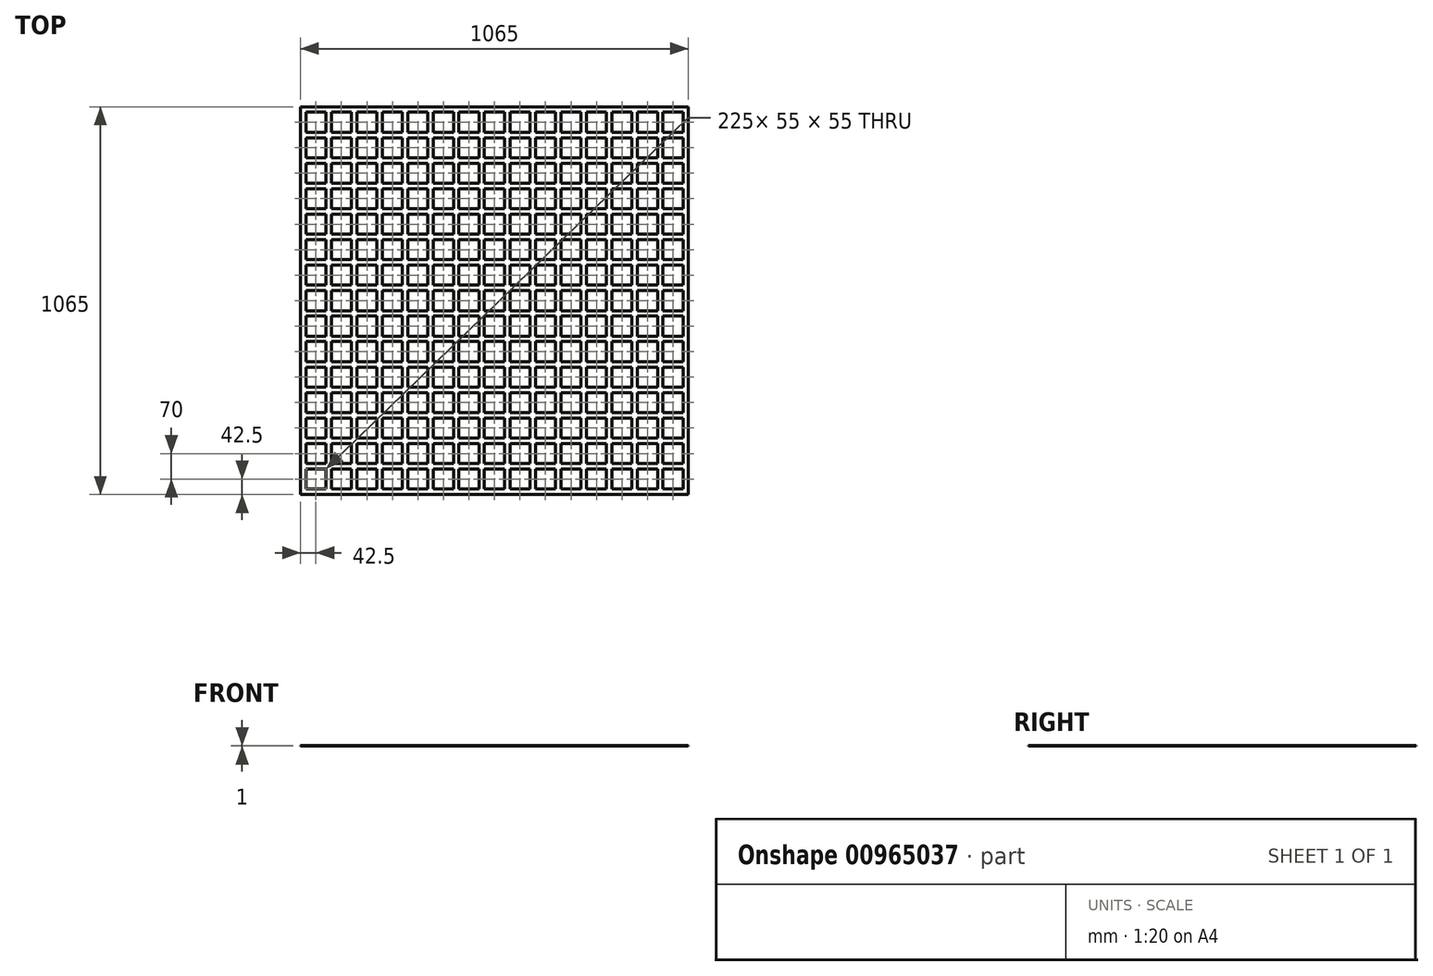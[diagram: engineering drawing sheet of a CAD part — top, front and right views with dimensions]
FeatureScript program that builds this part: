
annotation { "Feature Type Name" : "Feature", "Feature Type Description" : "" }
export const myFeature = defineFeature(function(context is Context, id is Id, definition is map)
    precondition{}
    {
        {
            var Q0;
            Q0=qCreatedBy(makeId("Top.planeOp"),FACE);
            var sketch = newSketch(context, id + "F0", { "sketchPlane" : qUnion([Q0])});
            skLineSegment(sketch, "E0.bottom", {"start": v(0, 0) * mm, "end": v(55, 0) * mm});
            skLineSegment(sketch, "E0.top", {"start": v(0, 55) * mm, "end": v(55, 55) * mm});
            skLineSegment(sketch, "E0.left", {"start": v(0, 0) * mm, "end": v(0, 55) * mm});
            skLineSegment(sketch, "E0.right", {"start": v(55, 0) * mm, "end": v(55, 55) * mm});
            skLineSegment(sketch, "E1.0.1.0", {"start": v(0, 70) * mm, "end": v(0, 125) * mm});
            skLineSegment(sketch, "E1.0.1.1", {"start": v(0, 125) * mm, "end": v(55, 125) * mm});
            skLineSegment(sketch, "E1.0.1.2", {"start": v(0, 70) * mm, "end": v(55, 70) * mm});
            skLineSegment(sketch, "E1.0.1.3", {"start": v(55, 70) * mm, "end": v(55, 125) * mm});
            skLineSegment(sketch, "E1.0.2.0", {"start": v(0, 140) * mm, "end": v(0, 195) * mm});
            skLineSegment(sketch, "E1.0.2.1", {"start": v(0, 195) * mm, "end": v(55, 195) * mm});
            skLineSegment(sketch, "E1.0.2.2", {"start": v(0, 140) * mm, "end": v(55, 140) * mm});
            skLineSegment(sketch, "E1.0.2.3", {"start": v(55, 140) * mm, "end": v(55, 195) * mm});
            skLineSegment(sketch, "E1.0.3.0", {"start": v(0, 210) * mm, "end": v(0, 265) * mm});
            skLineSegment(sketch, "E1.0.3.1", {"start": v(0, 265) * mm, "end": v(55, 265) * mm});
            skLineSegment(sketch, "E1.0.3.2", {"start": v(0, 210) * mm, "end": v(55, 210) * mm});
            skLineSegment(sketch, "E1.0.3.3", {"start": v(55, 210) * mm, "end": v(55, 265) * mm});
            skLineSegment(sketch, "E1.0.4.0", {"start": v(0, 280) * mm, "end": v(0, 335) * mm});
            skLineSegment(sketch, "E1.0.4.1", {"start": v(0, 335) * mm, "end": v(55, 335) * mm});
            skLineSegment(sketch, "E1.0.4.2", {"start": v(0, 280) * mm, "end": v(55, 280) * mm});
            skLineSegment(sketch, "E1.0.4.3", {"start": v(55, 280) * mm, "end": v(55, 335) * mm});
            skLineSegment(sketch, "E1.0.5.0", {"start": v(0, 350) * mm, "end": v(0, 405) * mm});
            skLineSegment(sketch, "E1.0.5.1", {"start": v(0, 405) * mm, "end": v(55, 405) * mm});
            skLineSegment(sketch, "E1.0.5.2", {"start": v(0, 350) * mm, "end": v(55, 350) * mm});
            skLineSegment(sketch, "E1.0.5.3", {"start": v(55, 350) * mm, "end": v(55, 405) * mm});
            skLineSegment(sketch, "E1.0.6.0", {"start": v(0, 420) * mm, "end": v(0, 475) * mm});
            skLineSegment(sketch, "E1.0.6.1", {"start": v(0, 475) * mm, "end": v(55, 475) * mm});
            skLineSegment(sketch, "E1.0.6.2", {"start": v(0, 420) * mm, "end": v(55, 420) * mm});
            skLineSegment(sketch, "E1.0.6.3", {"start": v(55, 420) * mm, "end": v(55, 475) * mm});
            skLineSegment(sketch, "E1.0.7.0", {"start": v(0, 490) * mm, "end": v(0, 545) * mm});
            skLineSegment(sketch, "E1.0.7.1", {"start": v(0, 545) * mm, "end": v(55, 545) * mm});
            skLineSegment(sketch, "E1.0.7.2", {"start": v(0, 490) * mm, "end": v(55, 490) * mm});
            skLineSegment(sketch, "E1.0.7.3", {"start": v(55, 490) * mm, "end": v(55, 545) * mm});
            skLineSegment(sketch, "E1.0.8.0", {"start": v(0, 560) * mm, "end": v(0, 615) * mm});
            skLineSegment(sketch, "E1.0.8.1", {"start": v(0, 615) * mm, "end": v(55, 615) * mm});
            skLineSegment(sketch, "E1.0.8.2", {"start": v(0, 560) * mm, "end": v(55, 560) * mm});
            skLineSegment(sketch, "E1.0.8.3", {"start": v(55, 560) * mm, "end": v(55, 615) * mm});
            skLineSegment(sketch, "E1.0.9.0", {"start": v(0, 630) * mm, "end": v(0, 685) * mm});
            skLineSegment(sketch, "E1.0.9.1", {"start": v(0, 685) * mm, "end": v(55, 685) * mm});
            skLineSegment(sketch, "E1.0.9.2", {"start": v(0, 630) * mm, "end": v(55, 630) * mm});
            skLineSegment(sketch, "E1.0.9.3", {"start": v(55, 630) * mm, "end": v(55, 685) * mm});
            skLineSegment(sketch, "E1.1.0.0", {"start": v(70, 0) * mm, "end": v(70, 55) * mm});
            skLineSegment(sketch, "E1.1.0.1", {"start": v(70, 55) * mm, "end": v(125, 55) * mm});
            skLineSegment(sketch, "E1.1.0.2", {"start": v(70, 0) * mm, "end": v(125, 0) * mm});
            skLineSegment(sketch, "E1.1.0.3", {"start": v(125, 0) * mm, "end": v(125, 55) * mm});
            skLineSegment(sketch, "E1.1.1.0", {"start": v(70, 70) * mm, "end": v(70, 125) * mm});
            skLineSegment(sketch, "E1.1.1.1", {"start": v(70, 125) * mm, "end": v(125, 125) * mm});
            skLineSegment(sketch, "E1.1.1.2", {"start": v(70, 70) * mm, "end": v(125, 70) * mm});
            skLineSegment(sketch, "E1.1.1.3", {"start": v(125, 70) * mm, "end": v(125, 125) * mm});
            skLineSegment(sketch, "E1.1.2.0", {"start": v(70, 140) * mm, "end": v(70, 195) * mm});
            skLineSegment(sketch, "E1.1.2.1", {"start": v(70, 195) * mm, "end": v(125, 195) * mm});
            skLineSegment(sketch, "E1.1.2.2", {"start": v(70, 140) * mm, "end": v(125, 140) * mm});
            skLineSegment(sketch, "E1.1.2.3", {"start": v(125, 140) * mm, "end": v(125, 195) * mm});
            skLineSegment(sketch, "E1.1.3.0", {"start": v(70, 210) * mm, "end": v(70, 265) * mm});
            skLineSegment(sketch, "E1.1.3.1", {"start": v(70, 265) * mm, "end": v(125, 265) * mm});
            skLineSegment(sketch, "E1.1.3.2", {"start": v(70, 210) * mm, "end": v(125, 210) * mm});
            skLineSegment(sketch, "E1.1.3.3", {"start": v(125, 210) * mm, "end": v(125, 265) * mm});
            skLineSegment(sketch, "E1.1.4.0", {"start": v(70, 280) * mm, "end": v(70, 335) * mm});
            skLineSegment(sketch, "E1.1.4.1", {"start": v(70, 335) * mm, "end": v(125, 335) * mm});
            skLineSegment(sketch, "E1.1.4.2", {"start": v(70, 280) * mm, "end": v(125, 280) * mm});
            skLineSegment(sketch, "E1.1.4.3", {"start": v(125, 280) * mm, "end": v(125, 335) * mm});
            skLineSegment(sketch, "E1.1.5.0", {"start": v(70, 350) * mm, "end": v(70, 405) * mm});
            skLineSegment(sketch, "E1.1.5.1", {"start": v(70, 405) * mm, "end": v(125, 405) * mm});
            skLineSegment(sketch, "E1.1.5.2", {"start": v(70, 350) * mm, "end": v(125, 350) * mm});
            skLineSegment(sketch, "E1.1.5.3", {"start": v(125, 350) * mm, "end": v(125, 405) * mm});
            skLineSegment(sketch, "E1.1.6.0", {"start": v(70, 420) * mm, "end": v(70, 475) * mm});
            skLineSegment(sketch, "E1.1.6.1", {"start": v(70, 475) * mm, "end": v(125, 475) * mm});
            skLineSegment(sketch, "E1.1.6.2", {"start": v(70, 420) * mm, "end": v(125, 420) * mm});
            skLineSegment(sketch, "E1.1.6.3", {"start": v(125, 420) * mm, "end": v(125, 475) * mm});
            skLineSegment(sketch, "E1.1.7.0", {"start": v(70, 490) * mm, "end": v(70, 545) * mm});
            skLineSegment(sketch, "E1.1.7.1", {"start": v(70, 545) * mm, "end": v(125, 545) * mm});
            skLineSegment(sketch, "E1.1.7.2", {"start": v(70, 490) * mm, "end": v(125, 490) * mm});
            skLineSegment(sketch, "E1.1.7.3", {"start": v(125, 490) * mm, "end": v(125, 545) * mm});
            skLineSegment(sketch, "E1.1.8.0", {"start": v(70, 560) * mm, "end": v(70, 615) * mm});
            skLineSegment(sketch, "E1.1.8.1", {"start": v(70, 615) * mm, "end": v(125, 615) * mm});
            skLineSegment(sketch, "E1.1.8.2", {"start": v(70, 560) * mm, "end": v(125, 560) * mm});
            skLineSegment(sketch, "E1.1.8.3", {"start": v(125, 560) * mm, "end": v(125, 615) * mm});
            skLineSegment(sketch, "E1.1.9.0", {"start": v(70, 630) * mm, "end": v(70, 685) * mm});
            skLineSegment(sketch, "E1.1.9.1", {"start": v(70, 685) * mm, "end": v(125, 685) * mm});
            skLineSegment(sketch, "E1.1.9.2", {"start": v(70, 630) * mm, "end": v(125, 630) * mm});
            skLineSegment(sketch, "E1.1.9.3", {"start": v(125, 630) * mm, "end": v(125, 685) * mm});
            skLineSegment(sketch, "E1.2.0.0", {"start": v(140, 0) * mm, "end": v(140, 55) * mm});
            skLineSegment(sketch, "E1.2.0.1", {"start": v(140, 55) * mm, "end": v(195, 55) * mm});
            skLineSegment(sketch, "E1.2.0.2", {"start": v(140, 0) * mm, "end": v(195, 0) * mm});
            skLineSegment(sketch, "E1.2.0.3", {"start": v(195, 0) * mm, "end": v(195, 55) * mm});
            skLineSegment(sketch, "E1.2.1.0", {"start": v(140, 70) * mm, "end": v(140, 125) * mm});
            skLineSegment(sketch, "E1.2.1.1", {"start": v(140, 125) * mm, "end": v(195, 125) * mm});
            skLineSegment(sketch, "E1.2.1.2", {"start": v(140, 70) * mm, "end": v(195, 70) * mm});
            skLineSegment(sketch, "E1.2.1.3", {"start": v(195, 70) * mm, "end": v(195, 125) * mm});
            skLineSegment(sketch, "E1.2.2.0", {"start": v(140, 140) * mm, "end": v(140, 195) * mm});
            skLineSegment(sketch, "E1.2.2.1", {"start": v(140, 195) * mm, "end": v(195, 195) * mm});
            skLineSegment(sketch, "E1.2.2.2", {"start": v(140, 140) * mm, "end": v(195, 140) * mm});
            skLineSegment(sketch, "E1.2.2.3", {"start": v(195, 140) * mm, "end": v(195, 195) * mm});
            skLineSegment(sketch, "E1.2.3.0", {"start": v(140, 210) * mm, "end": v(140, 265) * mm});
            skLineSegment(sketch, "E1.2.3.1", {"start": v(140, 265) * mm, "end": v(195, 265) * mm});
            skLineSegment(sketch, "E1.2.3.2", {"start": v(140, 210) * mm, "end": v(195, 210) * mm});
            skLineSegment(sketch, "E1.2.3.3", {"start": v(195, 210) * mm, "end": v(195, 265) * mm});
            skLineSegment(sketch, "E1.2.4.0", {"start": v(140, 280) * mm, "end": v(140, 335) * mm});
            skLineSegment(sketch, "E1.2.4.1", {"start": v(140, 335) * mm, "end": v(195, 335) * mm});
            skLineSegment(sketch, "E1.2.4.2", {"start": v(140, 280) * mm, "end": v(195, 280) * mm});
            skLineSegment(sketch, "E1.2.4.3", {"start": v(195, 280) * mm, "end": v(195, 335) * mm});
            skLineSegment(sketch, "E1.2.5.0", {"start": v(140, 350) * mm, "end": v(140, 405) * mm});
            skLineSegment(sketch, "E1.2.5.1", {"start": v(140, 405) * mm, "end": v(195, 405) * mm});
            skLineSegment(sketch, "E1.2.5.2", {"start": v(140, 350) * mm, "end": v(195, 350) * mm});
            skLineSegment(sketch, "E1.2.5.3", {"start": v(195, 350) * mm, "end": v(195, 405) * mm});
            skLineSegment(sketch, "E1.2.6.0", {"start": v(140, 420) * mm, "end": v(140, 475) * mm});
            skLineSegment(sketch, "E1.2.6.1", {"start": v(140, 475) * mm, "end": v(195, 475) * mm});
            skLineSegment(sketch, "E1.2.6.2", {"start": v(140, 420) * mm, "end": v(195, 420) * mm});
            skLineSegment(sketch, "E1.2.6.3", {"start": v(195, 420) * mm, "end": v(195, 475) * mm});
            skLineSegment(sketch, "E1.2.7.0", {"start": v(140, 490) * mm, "end": v(140, 545) * mm});
            skLineSegment(sketch, "E1.2.7.1", {"start": v(140, 545) * mm, "end": v(195, 545) * mm});
            skLineSegment(sketch, "E1.2.7.2", {"start": v(140, 490) * mm, "end": v(195, 490) * mm});
            skLineSegment(sketch, "E1.2.7.3", {"start": v(195, 490) * mm, "end": v(195, 545) * mm});
            skLineSegment(sketch, "E1.2.8.0", {"start": v(140, 560) * mm, "end": v(140, 615) * mm});
            skLineSegment(sketch, "E1.2.8.1", {"start": v(140, 615) * mm, "end": v(195, 615) * mm});
            skLineSegment(sketch, "E1.2.8.2", {"start": v(140, 560) * mm, "end": v(195, 560) * mm});
            skLineSegment(sketch, "E1.2.8.3", {"start": v(195, 560) * mm, "end": v(195, 615) * mm});
            skLineSegment(sketch, "E1.2.9.0", {"start": v(140, 630) * mm, "end": v(140, 685) * mm});
            skLineSegment(sketch, "E1.2.9.1", {"start": v(140, 685) * mm, "end": v(195, 685) * mm});
            skLineSegment(sketch, "E1.2.9.2", {"start": v(140, 630) * mm, "end": v(195, 630) * mm});
            skLineSegment(sketch, "E1.2.9.3", {"start": v(195, 630) * mm, "end": v(195, 685) * mm});
            skLineSegment(sketch, "E1.3.0.0", {"start": v(210, 0) * mm, "end": v(210, 55) * mm});
            skLineSegment(sketch, "E1.3.0.1", {"start": v(210, 55) * mm, "end": v(265, 55) * mm});
            skLineSegment(sketch, "E1.3.0.2", {"start": v(210, 0) * mm, "end": v(265, 0) * mm});
            skLineSegment(sketch, "E1.3.0.3", {"start": v(265, 0) * mm, "end": v(265, 55) * mm});
            skLineSegment(sketch, "E1.3.1.0", {"start": v(210, 70) * mm, "end": v(210, 125) * mm});
            skLineSegment(sketch, "E1.3.1.1", {"start": v(210, 125) * mm, "end": v(265, 125) * mm});
            skLineSegment(sketch, "E1.3.1.2", {"start": v(210, 70) * mm, "end": v(265, 70) * mm});
            skLineSegment(sketch, "E1.3.1.3", {"start": v(265, 70) * mm, "end": v(265, 125) * mm});
            skLineSegment(sketch, "E1.3.2.0", {"start": v(210, 140) * mm, "end": v(210, 195) * mm});
            skLineSegment(sketch, "E1.3.2.1", {"start": v(210, 195) * mm, "end": v(265, 195) * mm});
            skLineSegment(sketch, "E1.3.2.2", {"start": v(210, 140) * mm, "end": v(265, 140) * mm});
            skLineSegment(sketch, "E1.3.2.3", {"start": v(265, 140) * mm, "end": v(265, 195) * mm});
            skLineSegment(sketch, "E1.3.3.0", {"start": v(210, 210) * mm, "end": v(210, 265) * mm});
            skLineSegment(sketch, "E1.3.3.1", {"start": v(210, 265) * mm, "end": v(265, 265) * mm});
            skLineSegment(sketch, "E1.3.3.2", {"start": v(210, 210) * mm, "end": v(265, 210) * mm});
            skLineSegment(sketch, "E1.3.3.3", {"start": v(265, 210) * mm, "end": v(265, 265) * mm});
            skLineSegment(sketch, "E1.3.4.0", {"start": v(210, 280) * mm, "end": v(210, 335) * mm});
            skLineSegment(sketch, "E1.3.4.1", {"start": v(210, 335) * mm, "end": v(265, 335) * mm});
            skLineSegment(sketch, "E1.3.4.2", {"start": v(210, 280) * mm, "end": v(265, 280) * mm});
            skLineSegment(sketch, "E1.3.4.3", {"start": v(265, 280) * mm, "end": v(265, 335) * mm});
            skLineSegment(sketch, "E1.3.5.0", {"start": v(210, 350) * mm, "end": v(210, 405) * mm});
            skLineSegment(sketch, "E1.3.5.1", {"start": v(210, 405) * mm, "end": v(265, 405) * mm});
            skLineSegment(sketch, "E1.3.5.2", {"start": v(210, 350) * mm, "end": v(265, 350) * mm});
            skLineSegment(sketch, "E1.3.5.3", {"start": v(265, 350) * mm, "end": v(265, 405) * mm});
            skLineSegment(sketch, "E1.3.6.0", {"start": v(210, 420) * mm, "end": v(210, 475) * mm});
            skLineSegment(sketch, "E1.3.6.1", {"start": v(210, 475) * mm, "end": v(265, 475) * mm});
            skLineSegment(sketch, "E1.3.6.2", {"start": v(210, 420) * mm, "end": v(265, 420) * mm});
            skLineSegment(sketch, "E1.3.6.3", {"start": v(265, 420) * mm, "end": v(265, 475) * mm});
            skLineSegment(sketch, "E1.3.7.0", {"start": v(210, 490) * mm, "end": v(210, 545) * mm});
            skLineSegment(sketch, "E1.3.7.1", {"start": v(210, 545) * mm, "end": v(265, 545) * mm});
            skLineSegment(sketch, "E1.3.7.2", {"start": v(210, 490) * mm, "end": v(265, 490) * mm});
            skLineSegment(sketch, "E1.3.7.3", {"start": v(265, 490) * mm, "end": v(265, 545) * mm});
            skLineSegment(sketch, "E1.3.8.0", {"start": v(210, 560) * mm, "end": v(210, 615) * mm});
            skLineSegment(sketch, "E1.3.8.1", {"start": v(210, 615) * mm, "end": v(265, 615) * mm});
            skLineSegment(sketch, "E1.3.8.2", {"start": v(210, 560) * mm, "end": v(265, 560) * mm});
            skLineSegment(sketch, "E1.3.8.3", {"start": v(265, 560) * mm, "end": v(265, 615) * mm});
            skLineSegment(sketch, "E1.3.9.0", {"start": v(210, 630) * mm, "end": v(210, 685) * mm});
            skLineSegment(sketch, "E1.3.9.1", {"start": v(210, 685) * mm, "end": v(265, 685) * mm});
            skLineSegment(sketch, "E1.3.9.2", {"start": v(210, 630) * mm, "end": v(265, 630) * mm});
            skLineSegment(sketch, "E1.3.9.3", {"start": v(265, 630) * mm, "end": v(265, 685) * mm});
            skLineSegment(sketch, "E1.4.0.0", {"start": v(280, 0) * mm, "end": v(280, 55) * mm});
            skLineSegment(sketch, "E1.4.0.1", {"start": v(280, 55) * mm, "end": v(335, 55) * mm});
            skLineSegment(sketch, "E1.4.0.2", {"start": v(280, 0) * mm, "end": v(335, 0) * mm});
            skLineSegment(sketch, "E1.4.0.3", {"start": v(335, 0) * mm, "end": v(335, 55) * mm});
            skLineSegment(sketch, "E1.4.1.0", {"start": v(280, 70) * mm, "end": v(280, 125) * mm});
            skLineSegment(sketch, "E1.4.1.1", {"start": v(280, 125) * mm, "end": v(335, 125) * mm});
            skLineSegment(sketch, "E1.4.1.2", {"start": v(280, 70) * mm, "end": v(335, 70) * mm});
            skLineSegment(sketch, "E1.4.1.3", {"start": v(335, 70) * mm, "end": v(335, 125) * mm});
            skLineSegment(sketch, "E1.4.2.0", {"start": v(280, 140) * mm, "end": v(280, 195) * mm});
            skLineSegment(sketch, "E1.4.2.1", {"start": v(280, 195) * mm, "end": v(335, 195) * mm});
            skLineSegment(sketch, "E1.4.2.2", {"start": v(280, 140) * mm, "end": v(335, 140) * mm});
            skLineSegment(sketch, "E1.4.2.3", {"start": v(335, 140) * mm, "end": v(335, 195) * mm});
            skLineSegment(sketch, "E1.4.3.0", {"start": v(280, 210) * mm, "end": v(280, 265) * mm});
            skLineSegment(sketch, "E1.4.3.1", {"start": v(280, 265) * mm, "end": v(335, 265) * mm});
            skLineSegment(sketch, "E1.4.3.2", {"start": v(280, 210) * mm, "end": v(335, 210) * mm});
            skLineSegment(sketch, "E1.4.3.3", {"start": v(335, 210) * mm, "end": v(335, 265) * mm});
            skLineSegment(sketch, "E1.4.4.0", {"start": v(280, 280) * mm, "end": v(280, 335) * mm});
            skLineSegment(sketch, "E1.4.4.1", {"start": v(280, 335) * mm, "end": v(335, 335) * mm});
            skLineSegment(sketch, "E1.4.4.2", {"start": v(280, 280) * mm, "end": v(335, 280) * mm});
            skLineSegment(sketch, "E1.4.4.3", {"start": v(335, 280) * mm, "end": v(335, 335) * mm});
            skLineSegment(sketch, "E1.4.5.0", {"start": v(280, 350) * mm, "end": v(280, 405) * mm});
            skLineSegment(sketch, "E1.4.5.1", {"start": v(280, 405) * mm, "end": v(335, 405) * mm});
            skLineSegment(sketch, "E1.4.5.2", {"start": v(280, 350) * mm, "end": v(335, 350) * mm});
            skLineSegment(sketch, "E1.4.5.3", {"start": v(335, 350) * mm, "end": v(335, 405) * mm});
            skLineSegment(sketch, "E1.4.6.0", {"start": v(280, 420) * mm, "end": v(280, 475) * mm});
            skLineSegment(sketch, "E1.4.6.1", {"start": v(280, 475) * mm, "end": v(335, 475) * mm});
            skLineSegment(sketch, "E1.4.6.2", {"start": v(280, 420) * mm, "end": v(335, 420) * mm});
            skLineSegment(sketch, "E1.4.6.3", {"start": v(335, 420) * mm, "end": v(335, 475) * mm});
            skLineSegment(sketch, "E1.4.7.0", {"start": v(280, 490) * mm, "end": v(280, 545) * mm});
            skLineSegment(sketch, "E1.4.7.1", {"start": v(280, 545) * mm, "end": v(335, 545) * mm});
            skLineSegment(sketch, "E1.4.7.2", {"start": v(280, 490) * mm, "end": v(335, 490) * mm});
            skLineSegment(sketch, "E1.4.7.3", {"start": v(335, 490) * mm, "end": v(335, 545) * mm});
            skLineSegment(sketch, "E1.4.8.0", {"start": v(280, 560) * mm, "end": v(280, 615) * mm});
            skLineSegment(sketch, "E1.4.8.1", {"start": v(280, 615) * mm, "end": v(335, 615) * mm});
            skLineSegment(sketch, "E1.4.8.2", {"start": v(280, 560) * mm, "end": v(335, 560) * mm});
            skLineSegment(sketch, "E1.4.8.3", {"start": v(335, 560) * mm, "end": v(335, 615) * mm});
            skLineSegment(sketch, "E1.4.9.0", {"start": v(280, 630) * mm, "end": v(280, 685) * mm});
            skLineSegment(sketch, "E1.4.9.1", {"start": v(280, 685) * mm, "end": v(335, 685) * mm});
            skLineSegment(sketch, "E1.4.9.2", {"start": v(280, 630) * mm, "end": v(335, 630) * mm});
            skLineSegment(sketch, "E1.4.9.3", {"start": v(335, 630) * mm, "end": v(335, 685) * mm});
            skLineSegment(sketch, "E1.5.0.0", {"start": v(350, 0) * mm, "end": v(350, 55) * mm});
            skLineSegment(sketch, "E1.5.0.1", {"start": v(350, 55) * mm, "end": v(405, 55) * mm});
            skLineSegment(sketch, "E1.5.0.2", {"start": v(350, 0) * mm, "end": v(405, 0) * mm});
            skLineSegment(sketch, "E1.5.0.3", {"start": v(405, 0) * mm, "end": v(405, 55) * mm});
            skLineSegment(sketch, "E1.5.1.0", {"start": v(350, 70) * mm, "end": v(350, 125) * mm});
            skLineSegment(sketch, "E1.5.1.1", {"start": v(350, 125) * mm, "end": v(405, 125) * mm});
            skLineSegment(sketch, "E1.5.1.2", {"start": v(350, 70) * mm, "end": v(405, 70) * mm});
            skLineSegment(sketch, "E1.5.1.3", {"start": v(405, 70) * mm, "end": v(405, 125) * mm});
            skLineSegment(sketch, "E1.5.2.0", {"start": v(350, 140) * mm, "end": v(350, 195) * mm});
            skLineSegment(sketch, "E1.5.2.1", {"start": v(350, 195) * mm, "end": v(405, 195) * mm});
            skLineSegment(sketch, "E1.5.2.2", {"start": v(350, 140) * mm, "end": v(405, 140) * mm});
            skLineSegment(sketch, "E1.5.2.3", {"start": v(405, 140) * mm, "end": v(405, 195) * mm});
            skLineSegment(sketch, "E1.5.3.0", {"start": v(350, 210) * mm, "end": v(350, 265) * mm});
            skLineSegment(sketch, "E1.5.3.1", {"start": v(350, 265) * mm, "end": v(405, 265) * mm});
            skLineSegment(sketch, "E1.5.3.2", {"start": v(350, 210) * mm, "end": v(405, 210) * mm});
            skLineSegment(sketch, "E1.5.3.3", {"start": v(405, 210) * mm, "end": v(405, 265) * mm});
            skLineSegment(sketch, "E1.5.4.0", {"start": v(350, 280) * mm, "end": v(350, 335) * mm});
            skLineSegment(sketch, "E1.5.4.1", {"start": v(350, 335) * mm, "end": v(405, 335) * mm});
            skLineSegment(sketch, "E1.5.4.2", {"start": v(350, 280) * mm, "end": v(405, 280) * mm});
            skLineSegment(sketch, "E1.5.4.3", {"start": v(405, 280) * mm, "end": v(405, 335) * mm});
            skLineSegment(sketch, "E1.5.5.0", {"start": v(350, 350) * mm, "end": v(350, 405) * mm});
            skLineSegment(sketch, "E1.5.5.1", {"start": v(350, 405) * mm, "end": v(405, 405) * mm});
            skLineSegment(sketch, "E1.5.5.2", {"start": v(350, 350) * mm, "end": v(405, 350) * mm});
            skLineSegment(sketch, "E1.5.5.3", {"start": v(405, 350) * mm, "end": v(405, 405) * mm});
            skLineSegment(sketch, "E1.5.6.0", {"start": v(350, 420) * mm, "end": v(350, 475) * mm});
            skLineSegment(sketch, "E1.5.6.1", {"start": v(350, 475) * mm, "end": v(405, 475) * mm});
            skLineSegment(sketch, "E1.5.6.2", {"start": v(350, 420) * mm, "end": v(405, 420) * mm});
            skLineSegment(sketch, "E1.5.6.3", {"start": v(405, 420) * mm, "end": v(405, 475) * mm});
            skLineSegment(sketch, "E1.5.7.0", {"start": v(350, 490) * mm, "end": v(350, 545) * mm});
            skLineSegment(sketch, "E1.5.7.1", {"start": v(350, 545) * mm, "end": v(405, 545) * mm});
            skLineSegment(sketch, "E1.5.7.2", {"start": v(350, 490) * mm, "end": v(405, 490) * mm});
            skLineSegment(sketch, "E1.5.7.3", {"start": v(405, 490) * mm, "end": v(405, 545) * mm});
            skLineSegment(sketch, "E1.5.8.0", {"start": v(350, 560) * mm, "end": v(350, 615) * mm});
            skLineSegment(sketch, "E1.5.8.1", {"start": v(350, 615) * mm, "end": v(405, 615) * mm});
            skLineSegment(sketch, "E1.5.8.2", {"start": v(350, 560) * mm, "end": v(405, 560) * mm});
            skLineSegment(sketch, "E1.5.8.3", {"start": v(405, 560) * mm, "end": v(405, 615) * mm});
            skLineSegment(sketch, "E1.5.9.0", {"start": v(350, 630) * mm, "end": v(350, 685) * mm});
            skLineSegment(sketch, "E1.5.9.1", {"start": v(350, 685) * mm, "end": v(405, 685) * mm});
            skLineSegment(sketch, "E1.5.9.2", {"start": v(350, 630) * mm, "end": v(405, 630) * mm});
            skLineSegment(sketch, "E1.5.9.3", {"start": v(405, 630) * mm, "end": v(405, 685) * mm});
            skLineSegment(sketch, "E1.6.0.0", {"start": v(420, 0) * mm, "end": v(420, 55) * mm});
            skLineSegment(sketch, "E1.6.0.1", {"start": v(420, 55) * mm, "end": v(475, 55) * mm});
            skLineSegment(sketch, "E1.6.0.2", {"start": v(420, 0) * mm, "end": v(475, 0) * mm});
            skLineSegment(sketch, "E1.6.0.3", {"start": v(475, 0) * mm, "end": v(475, 55) * mm});
            skLineSegment(sketch, "E1.6.1.0", {"start": v(420, 70) * mm, "end": v(420, 125) * mm});
            skLineSegment(sketch, "E1.6.1.1", {"start": v(420, 125) * mm, "end": v(475, 125) * mm});
            skLineSegment(sketch, "E1.6.1.2", {"start": v(420, 70) * mm, "end": v(475, 70) * mm});
            skLineSegment(sketch, "E1.6.1.3", {"start": v(475, 70) * mm, "end": v(475, 125) * mm});
            skLineSegment(sketch, "E1.6.2.0", {"start": v(420, 140) * mm, "end": v(420, 195) * mm});
            skLineSegment(sketch, "E1.6.2.1", {"start": v(420, 195) * mm, "end": v(475, 195) * mm});
            skLineSegment(sketch, "E1.6.2.2", {"start": v(420, 140) * mm, "end": v(475, 140) * mm});
            skLineSegment(sketch, "E1.6.2.3", {"start": v(475, 140) * mm, "end": v(475, 195) * mm});
            skLineSegment(sketch, "E1.6.3.0", {"start": v(420, 210) * mm, "end": v(420, 265) * mm});
            skLineSegment(sketch, "E1.6.3.1", {"start": v(420, 265) * mm, "end": v(475, 265) * mm});
            skLineSegment(sketch, "E1.6.3.2", {"start": v(420, 210) * mm, "end": v(475, 210) * mm});
            skLineSegment(sketch, "E1.6.3.3", {"start": v(475, 210) * mm, "end": v(475, 265) * mm});
            skLineSegment(sketch, "E1.6.4.0", {"start": v(420, 280) * mm, "end": v(420, 335) * mm});
            skLineSegment(sketch, "E1.6.4.1", {"start": v(420, 335) * mm, "end": v(475, 335) * mm});
            skLineSegment(sketch, "E1.6.4.2", {"start": v(420, 280) * mm, "end": v(475, 280) * mm});
            skLineSegment(sketch, "E1.6.4.3", {"start": v(475, 280) * mm, "end": v(475, 335) * mm});
            skLineSegment(sketch, "E1.6.5.0", {"start": v(420, 350) * mm, "end": v(420, 405) * mm});
            skLineSegment(sketch, "E1.6.5.1", {"start": v(420, 405) * mm, "end": v(475, 405) * mm});
            skLineSegment(sketch, "E1.6.5.2", {"start": v(420, 350) * mm, "end": v(475, 350) * mm});
            skLineSegment(sketch, "E1.6.5.3", {"start": v(475, 350) * mm, "end": v(475, 405) * mm});
            skLineSegment(sketch, "E1.6.6.0", {"start": v(420, 420) * mm, "end": v(420, 475) * mm});
            skLineSegment(sketch, "E1.6.6.1", {"start": v(420, 475) * mm, "end": v(475, 475) * mm});
            skLineSegment(sketch, "E1.6.6.2", {"start": v(420, 420) * mm, "end": v(475, 420) * mm});
            skLineSegment(sketch, "E1.6.6.3", {"start": v(475, 420) * mm, "end": v(475, 475) * mm});
            skLineSegment(sketch, "E1.6.7.0", {"start": v(420, 490) * mm, "end": v(420, 545) * mm});
            skLineSegment(sketch, "E1.6.7.1", {"start": v(420, 545) * mm, "end": v(475, 545) * mm});
            skLineSegment(sketch, "E1.6.7.2", {"start": v(420, 490) * mm, "end": v(475, 490) * mm});
            skLineSegment(sketch, "E1.6.7.3", {"start": v(475, 490) * mm, "end": v(475, 545) * mm});
            skLineSegment(sketch, "E1.6.8.0", {"start": v(420, 560) * mm, "end": v(420, 615) * mm});
            skLineSegment(sketch, "E1.6.8.1", {"start": v(420, 615) * mm, "end": v(475, 615) * mm});
            skLineSegment(sketch, "E1.6.8.2", {"start": v(420, 560) * mm, "end": v(475, 560) * mm});
            skLineSegment(sketch, "E1.6.8.3", {"start": v(475, 560) * mm, "end": v(475, 615) * mm});
            skLineSegment(sketch, "E1.6.9.0", {"start": v(420, 630) * mm, "end": v(420, 685) * mm});
            skLineSegment(sketch, "E1.6.9.1", {"start": v(420, 685) * mm, "end": v(475, 685) * mm});
            skLineSegment(sketch, "E1.6.9.2", {"start": v(420, 630) * mm, "end": v(475, 630) * mm});
            skLineSegment(sketch, "E1.6.9.3", {"start": v(475, 630) * mm, "end": v(475, 685) * mm});
            skLineSegment(sketch, "E1.7.0.0", {"start": v(490, 0) * mm, "end": v(490, 55) * mm});
            skLineSegment(sketch, "E1.7.0.1", {"start": v(490, 55) * mm, "end": v(545, 55) * mm});
            skLineSegment(sketch, "E1.7.0.2", {"start": v(490, 0) * mm, "end": v(545, 0) * mm});
            skLineSegment(sketch, "E1.7.0.3", {"start": v(545, 0) * mm, "end": v(545, 55) * mm});
            skLineSegment(sketch, "E1.7.1.0", {"start": v(490, 70) * mm, "end": v(490, 125) * mm});
            skLineSegment(sketch, "E1.7.1.1", {"start": v(490, 125) * mm, "end": v(545, 125) * mm});
            skLineSegment(sketch, "E1.7.1.2", {"start": v(490, 70) * mm, "end": v(545, 70) * mm});
            skLineSegment(sketch, "E1.7.1.3", {"start": v(545, 70) * mm, "end": v(545, 125) * mm});
            skLineSegment(sketch, "E1.7.2.0", {"start": v(490, 140) * mm, "end": v(490, 195) * mm});
            skLineSegment(sketch, "E1.7.2.1", {"start": v(490, 195) * mm, "end": v(545, 195) * mm});
            skLineSegment(sketch, "E1.7.2.2", {"start": v(490, 140) * mm, "end": v(545, 140) * mm});
            skLineSegment(sketch, "E1.7.2.3", {"start": v(545, 140) * mm, "end": v(545, 195) * mm});
            skLineSegment(sketch, "E1.7.3.0", {"start": v(490, 210) * mm, "end": v(490, 265) * mm});
            skLineSegment(sketch, "E1.7.3.1", {"start": v(490, 265) * mm, "end": v(545, 265) * mm});
            skLineSegment(sketch, "E1.7.3.2", {"start": v(490, 210) * mm, "end": v(545, 210) * mm});
            skLineSegment(sketch, "E1.7.3.3", {"start": v(545, 210) * mm, "end": v(545, 265) * mm});
            skLineSegment(sketch, "E1.7.4.0", {"start": v(490, 280) * mm, "end": v(490, 335) * mm});
            skLineSegment(sketch, "E1.7.4.1", {"start": v(490, 335) * mm, "end": v(545, 335) * mm});
            skLineSegment(sketch, "E1.7.4.2", {"start": v(490, 280) * mm, "end": v(545, 280) * mm});
            skLineSegment(sketch, "E1.7.4.3", {"start": v(545, 280) * mm, "end": v(545, 335) * mm});
            skLineSegment(sketch, "E1.7.5.0", {"start": v(490, 350) * mm, "end": v(490, 405) * mm});
            skLineSegment(sketch, "E1.7.5.1", {"start": v(490, 405) * mm, "end": v(545, 405) * mm});
            skLineSegment(sketch, "E1.7.5.2", {"start": v(490, 350) * mm, "end": v(545, 350) * mm});
            skLineSegment(sketch, "E1.7.5.3", {"start": v(545, 350) * mm, "end": v(545, 405) * mm});
            skLineSegment(sketch, "E1.7.6.0", {"start": v(490, 420) * mm, "end": v(490, 475) * mm});
            skLineSegment(sketch, "E1.7.6.1", {"start": v(490, 475) * mm, "end": v(545, 475) * mm});
            skLineSegment(sketch, "E1.7.6.2", {"start": v(490, 420) * mm, "end": v(545, 420) * mm});
            skLineSegment(sketch, "E1.7.6.3", {"start": v(545, 420) * mm, "end": v(545, 475) * mm});
            skLineSegment(sketch, "E1.7.7.0", {"start": v(490, 490) * mm, "end": v(490, 545) * mm});
            skLineSegment(sketch, "E1.7.7.1", {"start": v(490, 545) * mm, "end": v(545, 545) * mm});
            skLineSegment(sketch, "E1.7.7.2", {"start": v(490, 490) * mm, "end": v(545, 490) * mm});
            skLineSegment(sketch, "E1.7.7.3", {"start": v(545, 490) * mm, "end": v(545, 545) * mm});
            skLineSegment(sketch, "E1.7.8.0", {"start": v(490, 560) * mm, "end": v(490, 615) * mm});
            skLineSegment(sketch, "E1.7.8.1", {"start": v(490, 615) * mm, "end": v(545, 615) * mm});
            skLineSegment(sketch, "E1.7.8.2", {"start": v(490, 560) * mm, "end": v(545, 560) * mm});
            skLineSegment(sketch, "E1.7.8.3", {"start": v(545, 560) * mm, "end": v(545, 615) * mm});
            skLineSegment(sketch, "E1.7.9.0", {"start": v(490, 630) * mm, "end": v(490, 685) * mm});
            skLineSegment(sketch, "E1.7.9.1", {"start": v(490, 685) * mm, "end": v(545, 685) * mm});
            skLineSegment(sketch, "E1.7.9.2", {"start": v(490, 630) * mm, "end": v(545, 630) * mm});
            skLineSegment(sketch, "E1.7.9.3", {"start": v(545, 630) * mm, "end": v(545, 685) * mm});
            skLineSegment(sketch, "E1.8.0.0", {"start": v(560, 0) * mm, "end": v(560, 55) * mm});
            skLineSegment(sketch, "E1.8.0.1", {"start": v(560, 55) * mm, "end": v(615, 55) * mm});
            skLineSegment(sketch, "E1.8.0.2", {"start": v(560, 0) * mm, "end": v(615, 0) * mm});
            skLineSegment(sketch, "E1.8.0.3", {"start": v(615, 0) * mm, "end": v(615, 55) * mm});
            skLineSegment(sketch, "E1.8.1.0", {"start": v(560, 70) * mm, "end": v(560, 125) * mm});
            skLineSegment(sketch, "E1.8.1.1", {"start": v(560, 125) * mm, "end": v(615, 125) * mm});
            skLineSegment(sketch, "E1.8.1.2", {"start": v(560, 70) * mm, "end": v(615, 70) * mm});
            skLineSegment(sketch, "E1.8.1.3", {"start": v(615, 70) * mm, "end": v(615, 125) * mm});
            skLineSegment(sketch, "E1.8.2.0", {"start": v(560, 140) * mm, "end": v(560, 195) * mm});
            skLineSegment(sketch, "E1.8.2.1", {"start": v(560, 195) * mm, "end": v(615, 195) * mm});
            skLineSegment(sketch, "E1.8.2.2", {"start": v(560, 140) * mm, "end": v(615, 140) * mm});
            skLineSegment(sketch, "E1.8.2.3", {"start": v(615, 140) * mm, "end": v(615, 195) * mm});
            skLineSegment(sketch, "E1.8.3.0", {"start": v(560, 210) * mm, "end": v(560, 265) * mm});
            skLineSegment(sketch, "E1.8.3.1", {"start": v(560, 265) * mm, "end": v(615, 265) * mm});
            skLineSegment(sketch, "E1.8.3.2", {"start": v(560, 210) * mm, "end": v(615, 210) * mm});
            skLineSegment(sketch, "E1.8.3.3", {"start": v(615, 210) * mm, "end": v(615, 265) * mm});
            skLineSegment(sketch, "E1.8.4.0", {"start": v(560, 280) * mm, "end": v(560, 335) * mm});
            skLineSegment(sketch, "E1.8.4.1", {"start": v(560, 335) * mm, "end": v(615, 335) * mm});
            skLineSegment(sketch, "E1.8.4.2", {"start": v(560, 280) * mm, "end": v(615, 280) * mm});
            skLineSegment(sketch, "E1.8.4.3", {"start": v(615, 280) * mm, "end": v(615, 335) * mm});
            skLineSegment(sketch, "E1.8.5.0", {"start": v(560, 350) * mm, "end": v(560, 405) * mm});
            skLineSegment(sketch, "E1.8.5.1", {"start": v(560, 405) * mm, "end": v(615, 405) * mm});
            skLineSegment(sketch, "E1.8.5.2", {"start": v(560, 350) * mm, "end": v(615, 350) * mm});
            skLineSegment(sketch, "E1.8.5.3", {"start": v(615, 350) * mm, "end": v(615, 405) * mm});
            skLineSegment(sketch, "E1.8.6.0", {"start": v(560, 420) * mm, "end": v(560, 475) * mm});
            skLineSegment(sketch, "E1.8.6.1", {"start": v(560, 475) * mm, "end": v(615, 475) * mm});
            skLineSegment(sketch, "E1.8.6.2", {"start": v(560, 420) * mm, "end": v(615, 420) * mm});
            skLineSegment(sketch, "E1.8.6.3", {"start": v(615, 420) * mm, "end": v(615, 475) * mm});
            skLineSegment(sketch, "E1.8.7.0", {"start": v(560, 490) * mm, "end": v(560, 545) * mm});
            skLineSegment(sketch, "E1.8.7.1", {"start": v(560, 545) * mm, "end": v(615, 545) * mm});
            skLineSegment(sketch, "E1.8.7.2", {"start": v(560, 490) * mm, "end": v(615, 490) * mm});
            skLineSegment(sketch, "E1.8.7.3", {"start": v(615, 490) * mm, "end": v(615, 545) * mm});
            skLineSegment(sketch, "E1.8.8.0", {"start": v(560, 560) * mm, "end": v(560, 615) * mm});
            skLineSegment(sketch, "E1.8.8.1", {"start": v(560, 615) * mm, "end": v(615, 615) * mm});
            skLineSegment(sketch, "E1.8.8.2", {"start": v(560, 560) * mm, "end": v(615, 560) * mm});
            skLineSegment(sketch, "E1.8.8.3", {"start": v(615, 560) * mm, "end": v(615, 615) * mm});
            skLineSegment(sketch, "E1.8.9.0", {"start": v(560, 630) * mm, "end": v(560, 685) * mm});
            skLineSegment(sketch, "E1.8.9.1", {"start": v(560, 685) * mm, "end": v(615, 685) * mm});
            skLineSegment(sketch, "E1.8.9.2", {"start": v(560, 630) * mm, "end": v(615, 630) * mm});
            skLineSegment(sketch, "E1.8.9.3", {"start": v(615, 630) * mm, "end": v(615, 685) * mm});
            skLineSegment(sketch, "E1.9.0.0", {"start": v(630, 0) * mm, "end": v(630, 55) * mm});
            skLineSegment(sketch, "E1.9.0.1", {"start": v(630, 55) * mm, "end": v(685, 55) * mm});
            skLineSegment(sketch, "E1.9.0.2", {"start": v(630, 0) * mm, "end": v(685, 0) * mm});
            skLineSegment(sketch, "E1.9.0.3", {"start": v(685, 0) * mm, "end": v(685, 55) * mm});
            skLineSegment(sketch, "E1.9.1.0", {"start": v(630, 70) * mm, "end": v(630, 125) * mm});
            skLineSegment(sketch, "E1.9.1.1", {"start": v(630, 125) * mm, "end": v(685, 125) * mm});
            skLineSegment(sketch, "E1.9.1.2", {"start": v(630, 70) * mm, "end": v(685, 70) * mm});
            skLineSegment(sketch, "E1.9.1.3", {"start": v(685, 70) * mm, "end": v(685, 125) * mm});
            skLineSegment(sketch, "E1.9.2.0", {"start": v(630, 140) * mm, "end": v(630, 195) * mm});
            skLineSegment(sketch, "E1.9.2.1", {"start": v(630, 195) * mm, "end": v(685, 195) * mm});
            skLineSegment(sketch, "E1.9.2.2", {"start": v(630, 140) * mm, "end": v(685, 140) * mm});
            skLineSegment(sketch, "E1.9.2.3", {"start": v(685, 140) * mm, "end": v(685, 195) * mm});
            skLineSegment(sketch, "E1.9.3.0", {"start": v(630, 210) * mm, "end": v(630, 265) * mm});
            skLineSegment(sketch, "E1.9.3.1", {"start": v(630, 265) * mm, "end": v(685, 265) * mm});
            skLineSegment(sketch, "E1.9.3.2", {"start": v(630, 210) * mm, "end": v(685, 210) * mm});
            skLineSegment(sketch, "E1.9.3.3", {"start": v(685, 210) * mm, "end": v(685, 265) * mm});
            skLineSegment(sketch, "E1.9.4.0", {"start": v(630, 280) * mm, "end": v(630, 335) * mm});
            skLineSegment(sketch, "E1.9.4.1", {"start": v(630, 335) * mm, "end": v(685, 335) * mm});
            skLineSegment(sketch, "E1.9.4.2", {"start": v(630, 280) * mm, "end": v(685, 280) * mm});
            skLineSegment(sketch, "E1.9.4.3", {"start": v(685, 280) * mm, "end": v(685, 335) * mm});
            skLineSegment(sketch, "E1.9.5.0", {"start": v(630, 350) * mm, "end": v(630, 405) * mm});
            skLineSegment(sketch, "E1.9.5.1", {"start": v(630, 405) * mm, "end": v(685, 405) * mm});
            skLineSegment(sketch, "E1.9.5.2", {"start": v(630, 350) * mm, "end": v(685, 350) * mm});
            skLineSegment(sketch, "E1.9.5.3", {"start": v(685, 350) * mm, "end": v(685, 405) * mm});
            skLineSegment(sketch, "E1.9.6.0", {"start": v(630, 420) * mm, "end": v(630, 475) * mm});
            skLineSegment(sketch, "E1.9.6.1", {"start": v(630, 475) * mm, "end": v(685, 475) * mm});
            skLineSegment(sketch, "E1.9.6.2", {"start": v(630, 420) * mm, "end": v(685, 420) * mm});
            skLineSegment(sketch, "E1.9.6.3", {"start": v(685, 420) * mm, "end": v(685, 475) * mm});
            skLineSegment(sketch, "E1.9.7.0", {"start": v(630, 490) * mm, "end": v(630, 545) * mm});
            skLineSegment(sketch, "E1.9.7.1", {"start": v(630, 545) * mm, "end": v(685, 545) * mm});
            skLineSegment(sketch, "E1.9.7.2", {"start": v(630, 490) * mm, "end": v(685, 490) * mm});
            skLineSegment(sketch, "E1.9.7.3", {"start": v(685, 490) * mm, "end": v(685, 545) * mm});
            skLineSegment(sketch, "E1.9.8.0", {"start": v(630, 560) * mm, "end": v(630, 615) * mm});
            skLineSegment(sketch, "E1.9.8.1", {"start": v(630, 615) * mm, "end": v(685, 615) * mm});
            skLineSegment(sketch, "E1.9.8.2", {"start": v(630, 560) * mm, "end": v(685, 560) * mm});
            skLineSegment(sketch, "E1.9.8.3", {"start": v(685, 560) * mm, "end": v(685, 615) * mm});
            skLineSegment(sketch, "E1.9.9.0", {"start": v(630, 630) * mm, "end": v(630, 685) * mm});
            skLineSegment(sketch, "E1.9.9.1", {"start": v(630, 685) * mm, "end": v(685, 685) * mm});
            skLineSegment(sketch, "E1.9.9.2", {"start": v(630, 630) * mm, "end": v(685, 630) * mm});
            skLineSegment(sketch, "E1.9.9.3", {"start": v(685, 630) * mm, "end": v(685, 685) * mm});
            skLineSegment(sketch, "E1.direction1", {"start": v(0, 0) * mm, "end": v(70, 0) * mm, "construction": true});
            skLineSegment(sketch, "E1.direction2", {"start": v(0, 0) * mm, "end": v(0, 70) * mm, "construction": true});
            skLineSegment(sketch, "E2.0.10.0", {"start": v(700, 0) * mm, "end": v(700, 55) * mm});
            skLineSegment(sketch, "E2.3.10.0", {"start": v(700, 55) * mm, "end": v(755, 55) * mm});
            skLineSegment(sketch, "E2.6.10.0", {"start": v(700, 0) * mm, "end": v(755, 0) * mm});
            skLineSegment(sketch, "E2.9.10.0", {"start": v(755, 0) * mm, "end": v(755, 55) * mm});
            skLineSegment(sketch, "E2.0.10.1", {"start": v(700, 70) * mm, "end": v(700, 125) * mm});
            skLineSegment(sketch, "E2.3.10.1", {"start": v(700, 125) * mm, "end": v(755, 125) * mm});
            skLineSegment(sketch, "E2.6.10.1", {"start": v(700, 70) * mm, "end": v(755, 70) * mm});
            skLineSegment(sketch, "E2.9.10.1", {"start": v(755, 70) * mm, "end": v(755, 125) * mm});
            skLineSegment(sketch, "E2.0.10.2", {"start": v(700, 140) * mm, "end": v(700, 195) * mm});
            skLineSegment(sketch, "E2.3.10.2", {"start": v(700, 195) * mm, "end": v(755, 195) * mm});
            skLineSegment(sketch, "E2.6.10.2", {"start": v(700, 140) * mm, "end": v(755, 140) * mm});
            skLineSegment(sketch, "E2.9.10.2", {"start": v(755, 140) * mm, "end": v(755, 195) * mm});
            skLineSegment(sketch, "E2.0.10.3", {"start": v(700, 210) * mm, "end": v(700, 265) * mm});
            skLineSegment(sketch, "E2.3.10.3", {"start": v(700, 265) * mm, "end": v(755, 265) * mm});
            skLineSegment(sketch, "E2.6.10.3", {"start": v(700, 210) * mm, "end": v(755, 210) * mm});
            skLineSegment(sketch, "E2.9.10.3", {"start": v(755, 210) * mm, "end": v(755, 265) * mm});
            skLineSegment(sketch, "E2.0.10.4", {"start": v(700, 280) * mm, "end": v(700, 335) * mm});
            skLineSegment(sketch, "E2.3.10.4", {"start": v(700, 335) * mm, "end": v(755, 335) * mm});
            skLineSegment(sketch, "E2.6.10.4", {"start": v(700, 280) * mm, "end": v(755, 280) * mm});
            skLineSegment(sketch, "E2.9.10.4", {"start": v(755, 280) * mm, "end": v(755, 335) * mm});
            skLineSegment(sketch, "E2.0.10.5", {"start": v(700, 350) * mm, "end": v(700, 405) * mm});
            skLineSegment(sketch, "E2.3.10.5", {"start": v(700, 405) * mm, "end": v(755, 405) * mm});
            skLineSegment(sketch, "E2.6.10.5", {"start": v(700, 350) * mm, "end": v(755, 350) * mm});
            skLineSegment(sketch, "E2.9.10.5", {"start": v(755, 350) * mm, "end": v(755, 405) * mm});
            skLineSegment(sketch, "E2.0.10.6", {"start": v(700, 420) * mm, "end": v(700, 475) * mm});
            skLineSegment(sketch, "E2.3.10.6", {"start": v(700, 475) * mm, "end": v(755, 475) * mm});
            skLineSegment(sketch, "E2.6.10.6", {"start": v(700, 420) * mm, "end": v(755, 420) * mm});
            skLineSegment(sketch, "E2.9.10.6", {"start": v(755, 420) * mm, "end": v(755, 475) * mm});
            skLineSegment(sketch, "E2.0.10.7", {"start": v(700, 490) * mm, "end": v(700, 545) * mm});
            skLineSegment(sketch, "E2.3.10.7", {"start": v(700, 545) * mm, "end": v(755, 545) * mm});
            skLineSegment(sketch, "E2.6.10.7", {"start": v(700, 490) * mm, "end": v(755, 490) * mm});
            skLineSegment(sketch, "E2.9.10.7", {"start": v(755, 490) * mm, "end": v(755, 545) * mm});
            skLineSegment(sketch, "E2.0.10.8", {"start": v(700, 560) * mm, "end": v(700, 615) * mm});
            skLineSegment(sketch, "E2.3.10.8", {"start": v(700, 615) * mm, "end": v(755, 615) * mm});
            skLineSegment(sketch, "E2.6.10.8", {"start": v(700, 560) * mm, "end": v(755, 560) * mm});
            skLineSegment(sketch, "E2.9.10.8", {"start": v(755, 560) * mm, "end": v(755, 615) * mm});
            skLineSegment(sketch, "E2.0.10.9", {"start": v(700, 630) * mm, "end": v(700, 685) * mm});
            skLineSegment(sketch, "E2.3.10.9", {"start": v(700, 685) * mm, "end": v(755, 685) * mm});
            skLineSegment(sketch, "E2.6.10.9", {"start": v(700, 630) * mm, "end": v(755, 630) * mm});
            skLineSegment(sketch, "E2.9.10.9", {"start": v(755, 630) * mm, "end": v(755, 685) * mm});
            skLineSegment(sketch, "E3.0.0.10", {"start": v(0, 700) * mm, "end": v(0, 755) * mm});
            skLineSegment(sketch, "E3.3.0.10", {"start": v(0, 755) * mm, "end": v(55, 755) * mm});
            skLineSegment(sketch, "E3.6.0.10", {"start": v(0, 700) * mm, "end": v(55, 700) * mm});
            skLineSegment(sketch, "E3.9.0.10", {"start": v(55, 700) * mm, "end": v(55, 755) * mm});
            skLineSegment(sketch, "E3.0.1.10", {"start": v(70, 700) * mm, "end": v(70, 755) * mm});
            skLineSegment(sketch, "E3.3.1.10", {"start": v(70, 755) * mm, "end": v(125, 755) * mm});
            skLineSegment(sketch, "E3.6.1.10", {"start": v(70, 700) * mm, "end": v(125, 700) * mm});
            skLineSegment(sketch, "E3.9.1.10", {"start": v(125, 700) * mm, "end": v(125, 755) * mm});
            skLineSegment(sketch, "E3.0.2.10", {"start": v(140, 700) * mm, "end": v(140, 755) * mm});
            skLineSegment(sketch, "E3.3.2.10", {"start": v(140, 755) * mm, "end": v(195, 755) * mm});
            skLineSegment(sketch, "E3.6.2.10", {"start": v(140, 700) * mm, "end": v(195, 700) * mm});
            skLineSegment(sketch, "E3.9.2.10", {"start": v(195, 700) * mm, "end": v(195, 755) * mm});
            skLineSegment(sketch, "E3.0.3.10", {"start": v(210, 700) * mm, "end": v(210, 755) * mm});
            skLineSegment(sketch, "E3.3.3.10", {"start": v(210, 755) * mm, "end": v(265, 755) * mm});
            skLineSegment(sketch, "E3.6.3.10", {"start": v(210, 700) * mm, "end": v(265, 700) * mm});
            skLineSegment(sketch, "E3.9.3.10", {"start": v(265, 700) * mm, "end": v(265, 755) * mm});
            skLineSegment(sketch, "E3.0.4.10", {"start": v(280, 700) * mm, "end": v(280, 755) * mm});
            skLineSegment(sketch, "E3.3.4.10", {"start": v(280, 755) * mm, "end": v(335, 755) * mm});
            skLineSegment(sketch, "E3.6.4.10", {"start": v(280, 700) * mm, "end": v(335, 700) * mm});
            skLineSegment(sketch, "E3.9.4.10", {"start": v(335, 700) * mm, "end": v(335, 755) * mm});
            skLineSegment(sketch, "E3.0.5.10", {"start": v(350, 700) * mm, "end": v(350, 755) * mm});
            skLineSegment(sketch, "E3.3.5.10", {"start": v(350, 755) * mm, "end": v(405, 755) * mm});
            skLineSegment(sketch, "E3.6.5.10", {"start": v(350, 700) * mm, "end": v(405, 700) * mm});
            skLineSegment(sketch, "E3.9.5.10", {"start": v(405, 700) * mm, "end": v(405, 755) * mm});
            skLineSegment(sketch, "E3.0.6.10", {"start": v(420, 700) * mm, "end": v(420, 755) * mm});
            skLineSegment(sketch, "E3.3.6.10", {"start": v(420, 755) * mm, "end": v(475, 755) * mm});
            skLineSegment(sketch, "E3.6.6.10", {"start": v(420, 700) * mm, "end": v(475, 700) * mm});
            skLineSegment(sketch, "E3.9.6.10", {"start": v(475, 700) * mm, "end": v(475, 755) * mm});
            skLineSegment(sketch, "E3.0.7.10", {"start": v(490, 700) * mm, "end": v(490, 755) * mm});
            skLineSegment(sketch, "E3.3.7.10", {"start": v(490, 755) * mm, "end": v(545, 755) * mm});
            skLineSegment(sketch, "E3.6.7.10", {"start": v(490, 700) * mm, "end": v(545, 700) * mm});
            skLineSegment(sketch, "E3.9.7.10", {"start": v(545, 700) * mm, "end": v(545, 755) * mm});
            skLineSegment(sketch, "E3.0.8.10", {"start": v(560, 700) * mm, "end": v(560, 755) * mm});
            skLineSegment(sketch, "E3.3.8.10", {"start": v(560, 755) * mm, "end": v(615, 755) * mm});
            skLineSegment(sketch, "E3.6.8.10", {"start": v(560, 700) * mm, "end": v(615, 700) * mm});
            skLineSegment(sketch, "E3.9.8.10", {"start": v(615, 700) * mm, "end": v(615, 755) * mm});
            skLineSegment(sketch, "E3.0.9.10", {"start": v(630, 700) * mm, "end": v(630, 755) * mm});
            skLineSegment(sketch, "E3.3.9.10", {"start": v(630, 755) * mm, "end": v(685, 755) * mm});
            skLineSegment(sketch, "E3.6.9.10", {"start": v(630, 700) * mm, "end": v(685, 700) * mm});
            skLineSegment(sketch, "E3.9.9.10", {"start": v(685, 700) * mm, "end": v(685, 755) * mm});
            skLineSegment(sketch, "E3.0.10.10", {"start": v(700, 700) * mm, "end": v(700, 755) * mm});
            skLineSegment(sketch, "E3.3.10.10", {"start": v(700, 755) * mm, "end": v(755, 755) * mm});
            skLineSegment(sketch, "E3.6.10.10", {"start": v(700, 700) * mm, "end": v(755, 700) * mm});
            skLineSegment(sketch, "E3.9.10.10", {"start": v(755, 700) * mm, "end": v(755, 755) * mm});
            skLineSegment(sketch, "E4.0.11.0", {"start": v(770, 0) * mm, "end": v(770, 55) * mm});
            skLineSegment(sketch, "E4.3.11.0", {"start": v(770, 55) * mm, "end": v(825, 55) * mm});
            skLineSegment(sketch, "E4.6.11.0", {"start": v(770, 0) * mm, "end": v(825, 0) * mm});
            skLineSegment(sketch, "E4.9.11.0", {"start": v(825, 0) * mm, "end": v(825, 55) * mm});
            skLineSegment(sketch, "E4.0.11.1", {"start": v(770, 70) * mm, "end": v(770, 125) * mm});
            skLineSegment(sketch, "E4.3.11.1", {"start": v(770, 125) * mm, "end": v(825, 125) * mm});
            skLineSegment(sketch, "E4.6.11.1", {"start": v(770, 70) * mm, "end": v(825, 70) * mm});
            skLineSegment(sketch, "E4.9.11.1", {"start": v(825, 70) * mm, "end": v(825, 125) * mm});
            skLineSegment(sketch, "E4.0.11.2", {"start": v(770, 140) * mm, "end": v(770, 195) * mm});
            skLineSegment(sketch, "E4.3.11.2", {"start": v(770, 195) * mm, "end": v(825, 195) * mm});
            skLineSegment(sketch, "E4.6.11.2", {"start": v(770, 140) * mm, "end": v(825, 140) * mm});
            skLineSegment(sketch, "E4.9.11.2", {"start": v(825, 140) * mm, "end": v(825, 195) * mm});
            skLineSegment(sketch, "E4.0.11.3", {"start": v(770, 210) * mm, "end": v(770, 265) * mm});
            skLineSegment(sketch, "E4.3.11.3", {"start": v(770, 265) * mm, "end": v(825, 265) * mm});
            skLineSegment(sketch, "E4.6.11.3", {"start": v(770, 210) * mm, "end": v(825, 210) * mm});
            skLineSegment(sketch, "E4.9.11.3", {"start": v(825, 210) * mm, "end": v(825, 265) * mm});
            skLineSegment(sketch, "E4.0.11.4", {"start": v(770, 280) * mm, "end": v(770, 335) * mm});
            skLineSegment(sketch, "E4.3.11.4", {"start": v(770, 335) * mm, "end": v(825, 335) * mm});
            skLineSegment(sketch, "E4.6.11.4", {"start": v(770, 280) * mm, "end": v(825, 280) * mm});
            skLineSegment(sketch, "E4.9.11.4", {"start": v(825, 280) * mm, "end": v(825, 335) * mm});
            skLineSegment(sketch, "E4.0.11.5", {"start": v(770, 350) * mm, "end": v(770, 405) * mm});
            skLineSegment(sketch, "E4.3.11.5", {"start": v(770, 405) * mm, "end": v(825, 405) * mm});
            skLineSegment(sketch, "E4.6.11.5", {"start": v(770, 350) * mm, "end": v(825, 350) * mm});
            skLineSegment(sketch, "E4.9.11.5", {"start": v(825, 350) * mm, "end": v(825, 405) * mm});
            skLineSegment(sketch, "E4.0.11.6", {"start": v(770, 420) * mm, "end": v(770, 475) * mm});
            skLineSegment(sketch, "E4.3.11.6", {"start": v(770, 475) * mm, "end": v(825, 475) * mm});
            skLineSegment(sketch, "E4.6.11.6", {"start": v(770, 420) * mm, "end": v(825, 420) * mm});
            skLineSegment(sketch, "E4.9.11.6", {"start": v(825, 420) * mm, "end": v(825, 475) * mm});
            skLineSegment(sketch, "E4.0.11.7", {"start": v(770, 490) * mm, "end": v(770, 545) * mm});
            skLineSegment(sketch, "E4.3.11.7", {"start": v(770, 545) * mm, "end": v(825, 545) * mm});
            skLineSegment(sketch, "E4.6.11.7", {"start": v(770, 490) * mm, "end": v(825, 490) * mm});
            skLineSegment(sketch, "E4.9.11.7", {"start": v(825, 490) * mm, "end": v(825, 545) * mm});
            skLineSegment(sketch, "E4.0.11.8", {"start": v(770, 560) * mm, "end": v(770, 615) * mm});
            skLineSegment(sketch, "E4.3.11.8", {"start": v(770, 615) * mm, "end": v(825, 615) * mm});
            skLineSegment(sketch, "E4.6.11.8", {"start": v(770, 560) * mm, "end": v(825, 560) * mm});
            skLineSegment(sketch, "E4.9.11.8", {"start": v(825, 560) * mm, "end": v(825, 615) * mm});
            skLineSegment(sketch, "E4.0.11.9", {"start": v(770, 630) * mm, "end": v(770, 685) * mm});
            skLineSegment(sketch, "E4.3.11.9", {"start": v(770, 685) * mm, "end": v(825, 685) * mm});
            skLineSegment(sketch, "E4.6.11.9", {"start": v(770, 630) * mm, "end": v(825, 630) * mm});
            skLineSegment(sketch, "E4.9.11.9", {"start": v(825, 630) * mm, "end": v(825, 685) * mm});
            skLineSegment(sketch, "E4.0.11.10", {"start": v(770, 700) * mm, "end": v(770, 755) * mm});
            skLineSegment(sketch, "E4.3.11.10", {"start": v(770, 755) * mm, "end": v(825, 755) * mm});
            skLineSegment(sketch, "E4.6.11.10", {"start": v(770, 700) * mm, "end": v(825, 700) * mm});
            skLineSegment(sketch, "E4.9.11.10", {"start": v(825, 700) * mm, "end": v(825, 755) * mm});
            skLineSegment(sketch, "E5.0.0.11", {"start": v(0, 770) * mm, "end": v(0, 825) * mm});
            skLineSegment(sketch, "E5.3.0.11", {"start": v(0, 825) * mm, "end": v(55, 825) * mm});
            skLineSegment(sketch, "E5.6.0.11", {"start": v(0, 770) * mm, "end": v(55, 770) * mm});
            skLineSegment(sketch, "E5.9.0.11", {"start": v(55, 770) * mm, "end": v(55, 825) * mm});
            skLineSegment(sketch, "E5.0.1.11", {"start": v(70, 770) * mm, "end": v(70, 825) * mm});
            skLineSegment(sketch, "E5.3.1.11", {"start": v(70, 825) * mm, "end": v(125, 825) * mm});
            skLineSegment(sketch, "E5.6.1.11", {"start": v(70, 770) * mm, "end": v(125, 770) * mm});
            skLineSegment(sketch, "E5.9.1.11", {"start": v(125, 770) * mm, "end": v(125, 825) * mm});
            skLineSegment(sketch, "E5.0.2.11", {"start": v(140, 770) * mm, "end": v(140, 825) * mm});
            skLineSegment(sketch, "E5.3.2.11", {"start": v(140, 825) * mm, "end": v(195, 825) * mm});
            skLineSegment(sketch, "E5.6.2.11", {"start": v(140, 770) * mm, "end": v(195, 770) * mm});
            skLineSegment(sketch, "E5.9.2.11", {"start": v(195, 770) * mm, "end": v(195, 825) * mm});
            skLineSegment(sketch, "E5.0.3.11", {"start": v(210, 770) * mm, "end": v(210, 825) * mm});
            skLineSegment(sketch, "E5.3.3.11", {"start": v(210, 825) * mm, "end": v(265, 825) * mm});
            skLineSegment(sketch, "E5.6.3.11", {"start": v(210, 770) * mm, "end": v(265, 770) * mm});
            skLineSegment(sketch, "E5.9.3.11", {"start": v(265, 770) * mm, "end": v(265, 825) * mm});
            skLineSegment(sketch, "E5.0.4.11", {"start": v(280, 770) * mm, "end": v(280, 825) * mm});
            skLineSegment(sketch, "E5.3.4.11", {"start": v(280, 825) * mm, "end": v(335, 825) * mm});
            skLineSegment(sketch, "E5.6.4.11", {"start": v(280, 770) * mm, "end": v(335, 770) * mm});
            skLineSegment(sketch, "E5.9.4.11", {"start": v(335, 770) * mm, "end": v(335, 825) * mm});
            skLineSegment(sketch, "E5.0.5.11", {"start": v(350, 770) * mm, "end": v(350, 825) * mm});
            skLineSegment(sketch, "E5.3.5.11", {"start": v(350, 825) * mm, "end": v(405, 825) * mm});
            skLineSegment(sketch, "E5.6.5.11", {"start": v(350, 770) * mm, "end": v(405, 770) * mm});
            skLineSegment(sketch, "E5.9.5.11", {"start": v(405, 770) * mm, "end": v(405, 825) * mm});
            skLineSegment(sketch, "E5.0.6.11", {"start": v(420, 770) * mm, "end": v(420, 825) * mm});
            skLineSegment(sketch, "E5.3.6.11", {"start": v(420, 825) * mm, "end": v(475, 825) * mm});
            skLineSegment(sketch, "E5.6.6.11", {"start": v(420, 770) * mm, "end": v(475, 770) * mm});
            skLineSegment(sketch, "E5.9.6.11", {"start": v(475, 770) * mm, "end": v(475, 825) * mm});
            skLineSegment(sketch, "E5.0.7.11", {"start": v(490, 770) * mm, "end": v(490, 825) * mm});
            skLineSegment(sketch, "E5.3.7.11", {"start": v(490, 825) * mm, "end": v(545, 825) * mm});
            skLineSegment(sketch, "E5.6.7.11", {"start": v(490, 770) * mm, "end": v(545, 770) * mm});
            skLineSegment(sketch, "E5.9.7.11", {"start": v(545, 770) * mm, "end": v(545, 825) * mm});
            skLineSegment(sketch, "E5.0.8.11", {"start": v(560, 770) * mm, "end": v(560, 825) * mm});
            skLineSegment(sketch, "E5.3.8.11", {"start": v(560, 825) * mm, "end": v(615, 825) * mm});
            skLineSegment(sketch, "E5.6.8.11", {"start": v(560, 770) * mm, "end": v(615, 770) * mm});
            skLineSegment(sketch, "E5.9.8.11", {"start": v(615, 770) * mm, "end": v(615, 825) * mm});
            skLineSegment(sketch, "E5.0.9.11", {"start": v(630, 770) * mm, "end": v(630, 825) * mm});
            skLineSegment(sketch, "E5.3.9.11", {"start": v(630, 825) * mm, "end": v(685, 825) * mm});
            skLineSegment(sketch, "E5.6.9.11", {"start": v(630, 770) * mm, "end": v(685, 770) * mm});
            skLineSegment(sketch, "E5.9.9.11", {"start": v(685, 770) * mm, "end": v(685, 825) * mm});
            skLineSegment(sketch, "E5.0.10.11", {"start": v(700, 770) * mm, "end": v(700, 825) * mm});
            skLineSegment(sketch, "E5.3.10.11", {"start": v(700, 825) * mm, "end": v(755, 825) * mm});
            skLineSegment(sketch, "E5.6.10.11", {"start": v(700, 770) * mm, "end": v(755, 770) * mm});
            skLineSegment(sketch, "E5.9.10.11", {"start": v(755, 770) * mm, "end": v(755, 825) * mm});
            skLineSegment(sketch, "E5.0.11.11", {"start": v(770, 770) * mm, "end": v(770, 825) * mm});
            skLineSegment(sketch, "E5.3.11.11", {"start": v(770, 825) * mm, "end": v(825, 825) * mm});
            skLineSegment(sketch, "E5.6.11.11", {"start": v(770, 770) * mm, "end": v(825, 770) * mm});
            skLineSegment(sketch, "E5.9.11.11", {"start": v(825, 770) * mm, "end": v(825, 825) * mm});
            skLineSegment(sketch, "E6.bottom", {"start": v(-15, -15) * mm, "end": v(1050, -15) * mm});
            skLineSegment(sketch, "E6.top", {"start": v(-15, 1050) * mm, "end": v(1050, 1050) * mm});
            skLineSegment(sketch, "E6.left", {"start": v(-15, -15) * mm, "end": v(-15, 1050) * mm});
            skLineSegment(sketch, "E6.right", {"start": v(1050, -15) * mm, "end": v(1050, 1050) * mm});
            skLineSegment(sketch, "E7.0.12.0", {"start": v(840, 0) * mm, "end": v(840, 55) * mm});
            skLineSegment(sketch, "E7.3.12.0", {"start": v(840, 55) * mm, "end": v(895, 55) * mm});
            skLineSegment(sketch, "E7.6.12.0", {"start": v(840, 0) * mm, "end": v(895, 0) * mm});
            skLineSegment(sketch, "E7.9.12.0", {"start": v(895, 0) * mm, "end": v(895, 55) * mm});
            skLineSegment(sketch, "E7.0.12.1", {"start": v(840, 70) * mm, "end": v(840, 125) * mm});
            skLineSegment(sketch, "E7.3.12.1", {"start": v(840, 125) * mm, "end": v(895, 125) * mm});
            skLineSegment(sketch, "E7.6.12.1", {"start": v(840, 70) * mm, "end": v(895, 70) * mm});
            skLineSegment(sketch, "E7.9.12.1", {"start": v(895, 70) * mm, "end": v(895, 125) * mm});
            skLineSegment(sketch, "E7.0.12.2", {"start": v(840, 140) * mm, "end": v(840, 195) * mm});
            skLineSegment(sketch, "E7.3.12.2", {"start": v(840, 195) * mm, "end": v(895, 195) * mm});
            skLineSegment(sketch, "E7.6.12.2", {"start": v(840, 140) * mm, "end": v(895, 140) * mm});
            skLineSegment(sketch, "E7.9.12.2", {"start": v(895, 140) * mm, "end": v(895, 195) * mm});
            skLineSegment(sketch, "E7.0.12.3", {"start": v(840, 210) * mm, "end": v(840, 265) * mm});
            skLineSegment(sketch, "E7.3.12.3", {"start": v(840, 265) * mm, "end": v(895, 265) * mm});
            skLineSegment(sketch, "E7.6.12.3", {"start": v(840, 210) * mm, "end": v(895, 210) * mm});
            skLineSegment(sketch, "E7.9.12.3", {"start": v(895, 210) * mm, "end": v(895, 265) * mm});
            skLineSegment(sketch, "E7.0.12.4", {"start": v(840, 280) * mm, "end": v(840, 335) * mm});
            skLineSegment(sketch, "E7.3.12.4", {"start": v(840, 335) * mm, "end": v(895, 335) * mm});
            skLineSegment(sketch, "E7.6.12.4", {"start": v(840, 280) * mm, "end": v(895, 280) * mm});
            skLineSegment(sketch, "E7.9.12.4", {"start": v(895, 280) * mm, "end": v(895, 335) * mm});
            skLineSegment(sketch, "E7.0.12.5", {"start": v(840, 350) * mm, "end": v(840, 405) * mm});
            skLineSegment(sketch, "E7.3.12.5", {"start": v(840, 405) * mm, "end": v(895, 405) * mm});
            skLineSegment(sketch, "E7.6.12.5", {"start": v(840, 350) * mm, "end": v(895, 350) * mm});
            skLineSegment(sketch, "E7.9.12.5", {"start": v(895, 350) * mm, "end": v(895, 405) * mm});
            skLineSegment(sketch, "E7.0.12.6", {"start": v(840, 420) * mm, "end": v(840, 475) * mm});
            skLineSegment(sketch, "E7.3.12.6", {"start": v(840, 475) * mm, "end": v(895, 475) * mm});
            skLineSegment(sketch, "E7.6.12.6", {"start": v(840, 420) * mm, "end": v(895, 420) * mm});
            skLineSegment(sketch, "E7.9.12.6", {"start": v(895, 420) * mm, "end": v(895, 475) * mm});
            skLineSegment(sketch, "E7.0.12.7", {"start": v(840, 490) * mm, "end": v(840, 545) * mm});
            skLineSegment(sketch, "E7.3.12.7", {"start": v(840, 545) * mm, "end": v(895, 545) * mm});
            skLineSegment(sketch, "E7.6.12.7", {"start": v(840, 490) * mm, "end": v(895, 490) * mm});
            skLineSegment(sketch, "E7.9.12.7", {"start": v(895, 490) * mm, "end": v(895, 545) * mm});
            skLineSegment(sketch, "E7.0.12.8", {"start": v(840, 560) * mm, "end": v(840, 615) * mm});
            skLineSegment(sketch, "E7.3.12.8", {"start": v(840, 615) * mm, "end": v(895, 615) * mm});
            skLineSegment(sketch, "E7.6.12.8", {"start": v(840, 560) * mm, "end": v(895, 560) * mm});
            skLineSegment(sketch, "E7.9.12.8", {"start": v(895, 560) * mm, "end": v(895, 615) * mm});
            skLineSegment(sketch, "E7.0.12.9", {"start": v(840, 630) * mm, "end": v(840, 685) * mm});
            skLineSegment(sketch, "E7.3.12.9", {"start": v(840, 685) * mm, "end": v(895, 685) * mm});
            skLineSegment(sketch, "E7.6.12.9", {"start": v(840, 630) * mm, "end": v(895, 630) * mm});
            skLineSegment(sketch, "E7.9.12.9", {"start": v(895, 630) * mm, "end": v(895, 685) * mm});
            skLineSegment(sketch, "E7.0.12.10", {"start": v(840, 700) * mm, "end": v(840, 755) * mm});
            skLineSegment(sketch, "E7.3.12.10", {"start": v(840, 755) * mm, "end": v(895, 755) * mm});
            skLineSegment(sketch, "E7.6.12.10", {"start": v(840, 700) * mm, "end": v(895, 700) * mm});
            skLineSegment(sketch, "E7.9.12.10", {"start": v(895, 700) * mm, "end": v(895, 755) * mm});
            skLineSegment(sketch, "E7.0.12.11", {"start": v(840, 770) * mm, "end": v(840, 825) * mm});
            skLineSegment(sketch, "E7.3.12.11", {"start": v(840, 825) * mm, "end": v(895, 825) * mm});
            skLineSegment(sketch, "E7.6.12.11", {"start": v(840, 770) * mm, "end": v(895, 770) * mm});
            skLineSegment(sketch, "E7.9.12.11", {"start": v(895, 770) * mm, "end": v(895, 825) * mm});
            skLineSegment(sketch, "E7.0.13.0", {"start": v(910, 0) * mm, "end": v(910, 55) * mm});
            skLineSegment(sketch, "E7.3.13.0", {"start": v(910, 55) * mm, "end": v(965, 55) * mm});
            skLineSegment(sketch, "E7.6.13.0", {"start": v(910, 0) * mm, "end": v(965, 0) * mm});
            skLineSegment(sketch, "E7.9.13.0", {"start": v(965, 0) * mm, "end": v(965, 55) * mm});
            skLineSegment(sketch, "E7.0.13.1", {"start": v(910, 70) * mm, "end": v(910, 125) * mm});
            skLineSegment(sketch, "E7.3.13.1", {"start": v(910, 125) * mm, "end": v(965, 125) * mm});
            skLineSegment(sketch, "E7.6.13.1", {"start": v(910, 70) * mm, "end": v(965, 70) * mm});
            skLineSegment(sketch, "E7.9.13.1", {"start": v(965, 70) * mm, "end": v(965, 125) * mm});
            skLineSegment(sketch, "E7.0.13.2", {"start": v(910, 140) * mm, "end": v(910, 195) * mm});
            skLineSegment(sketch, "E7.3.13.2", {"start": v(910, 195) * mm, "end": v(965, 195) * mm});
            skLineSegment(sketch, "E7.6.13.2", {"start": v(910, 140) * mm, "end": v(965, 140) * mm});
            skLineSegment(sketch, "E7.9.13.2", {"start": v(965, 140) * mm, "end": v(965, 195) * mm});
            skLineSegment(sketch, "E7.0.13.3", {"start": v(910, 210) * mm, "end": v(910, 265) * mm});
            skLineSegment(sketch, "E7.3.13.3", {"start": v(910, 265) * mm, "end": v(965, 265) * mm});
            skLineSegment(sketch, "E7.6.13.3", {"start": v(910, 210) * mm, "end": v(965, 210) * mm});
            skLineSegment(sketch, "E7.9.13.3", {"start": v(965, 210) * mm, "end": v(965, 265) * mm});
            skLineSegment(sketch, "E7.0.13.4", {"start": v(910, 280) * mm, "end": v(910, 335) * mm});
            skLineSegment(sketch, "E7.3.13.4", {"start": v(910, 335) * mm, "end": v(965, 335) * mm});
            skLineSegment(sketch, "E7.6.13.4", {"start": v(910, 280) * mm, "end": v(965, 280) * mm});
            skLineSegment(sketch, "E7.9.13.4", {"start": v(965, 280) * mm, "end": v(965, 335) * mm});
            skLineSegment(sketch, "E7.0.13.5", {"start": v(910, 350) * mm, "end": v(910, 405) * mm});
            skLineSegment(sketch, "E7.3.13.5", {"start": v(910, 405) * mm, "end": v(965, 405) * mm});
            skLineSegment(sketch, "E7.6.13.5", {"start": v(910, 350) * mm, "end": v(965, 350) * mm});
            skLineSegment(sketch, "E7.9.13.5", {"start": v(965, 350) * mm, "end": v(965, 405) * mm});
            skLineSegment(sketch, "E7.0.13.6", {"start": v(910, 420) * mm, "end": v(910, 475) * mm});
            skLineSegment(sketch, "E7.3.13.6", {"start": v(910, 475) * mm, "end": v(965, 475) * mm});
            skLineSegment(sketch, "E7.6.13.6", {"start": v(910, 420) * mm, "end": v(965, 420) * mm});
            skLineSegment(sketch, "E7.9.13.6", {"start": v(965, 420) * mm, "end": v(965, 475) * mm});
            skLineSegment(sketch, "E7.0.13.7", {"start": v(910, 490) * mm, "end": v(910, 545) * mm});
            skLineSegment(sketch, "E7.3.13.7", {"start": v(910, 545) * mm, "end": v(965, 545) * mm});
            skLineSegment(sketch, "E7.6.13.7", {"start": v(910, 490) * mm, "end": v(965, 490) * mm});
            skLineSegment(sketch, "E7.9.13.7", {"start": v(965, 490) * mm, "end": v(965, 545) * mm});
            skLineSegment(sketch, "E7.0.13.8", {"start": v(910, 560) * mm, "end": v(910, 615) * mm});
            skLineSegment(sketch, "E7.3.13.8", {"start": v(910, 615) * mm, "end": v(965, 615) * mm});
            skLineSegment(sketch, "E7.6.13.8", {"start": v(910, 560) * mm, "end": v(965, 560) * mm});
            skLineSegment(sketch, "E7.9.13.8", {"start": v(965, 560) * mm, "end": v(965, 615) * mm});
            skLineSegment(sketch, "E7.0.13.9", {"start": v(910, 630) * mm, "end": v(910, 685) * mm});
            skLineSegment(sketch, "E7.3.13.9", {"start": v(910, 685) * mm, "end": v(965, 685) * mm});
            skLineSegment(sketch, "E7.6.13.9", {"start": v(910, 630) * mm, "end": v(965, 630) * mm});
            skLineSegment(sketch, "E7.9.13.9", {"start": v(965, 630) * mm, "end": v(965, 685) * mm});
            skLineSegment(sketch, "E7.0.13.10", {"start": v(910, 700) * mm, "end": v(910, 755) * mm});
            skLineSegment(sketch, "E7.3.13.10", {"start": v(910, 755) * mm, "end": v(965, 755) * mm});
            skLineSegment(sketch, "E7.6.13.10", {"start": v(910, 700) * mm, "end": v(965, 700) * mm});
            skLineSegment(sketch, "E7.9.13.10", {"start": v(965, 700) * mm, "end": v(965, 755) * mm});
            skLineSegment(sketch, "E7.0.13.11", {"start": v(910, 770) * mm, "end": v(910, 825) * mm});
            skLineSegment(sketch, "E7.3.13.11", {"start": v(910, 825) * mm, "end": v(965, 825) * mm});
            skLineSegment(sketch, "E7.6.13.11", {"start": v(910, 770) * mm, "end": v(965, 770) * mm});
            skLineSegment(sketch, "E7.9.13.11", {"start": v(965, 770) * mm, "end": v(965, 825) * mm});
            skLineSegment(sketch, "E7.0.14.0", {"start": v(980, 0) * mm, "end": v(980, 55) * mm});
            skLineSegment(sketch, "E7.3.14.0", {"start": v(980, 55) * mm, "end": v(1035, 55) * mm});
            skLineSegment(sketch, "E7.6.14.0", {"start": v(980, 0) * mm, "end": v(1035, 0) * mm});
            skLineSegment(sketch, "E7.9.14.0", {"start": v(1035, 0) * mm, "end": v(1035, 55) * mm});
            skLineSegment(sketch, "E7.0.14.1", {"start": v(980, 70) * mm, "end": v(980, 125) * mm});
            skLineSegment(sketch, "E7.3.14.1", {"start": v(980, 125) * mm, "end": v(1035, 125) * mm});
            skLineSegment(sketch, "E7.6.14.1", {"start": v(980, 70) * mm, "end": v(1035, 70) * mm});
            skLineSegment(sketch, "E7.9.14.1", {"start": v(1035, 70) * mm, "end": v(1035, 125) * mm});
            skLineSegment(sketch, "E7.0.14.2", {"start": v(980, 140) * mm, "end": v(980, 195) * mm});
            skLineSegment(sketch, "E7.3.14.2", {"start": v(980, 195) * mm, "end": v(1035, 195) * mm});
            skLineSegment(sketch, "E7.6.14.2", {"start": v(980, 140) * mm, "end": v(1035, 140) * mm});
            skLineSegment(sketch, "E7.9.14.2", {"start": v(1035, 140) * mm, "end": v(1035, 195) * mm});
            skLineSegment(sketch, "E7.0.14.3", {"start": v(980, 210) * mm, "end": v(980, 265) * mm});
            skLineSegment(sketch, "E7.3.14.3", {"start": v(980, 265) * mm, "end": v(1035, 265) * mm});
            skLineSegment(sketch, "E7.6.14.3", {"start": v(980, 210) * mm, "end": v(1035, 210) * mm});
            skLineSegment(sketch, "E7.9.14.3", {"start": v(1035, 210) * mm, "end": v(1035, 265) * mm});
            skLineSegment(sketch, "E7.0.14.4", {"start": v(980, 280) * mm, "end": v(980, 335) * mm});
            skLineSegment(sketch, "E7.3.14.4", {"start": v(980, 335) * mm, "end": v(1035, 335) * mm});
            skLineSegment(sketch, "E7.6.14.4", {"start": v(980, 280) * mm, "end": v(1035, 280) * mm});
            skLineSegment(sketch, "E7.9.14.4", {"start": v(1035, 280) * mm, "end": v(1035, 335) * mm});
            skLineSegment(sketch, "E7.0.14.5", {"start": v(980, 350) * mm, "end": v(980, 405) * mm});
            skLineSegment(sketch, "E7.3.14.5", {"start": v(980, 405) * mm, "end": v(1035, 405) * mm});
            skLineSegment(sketch, "E7.6.14.5", {"start": v(980, 350) * mm, "end": v(1035, 350) * mm});
            skLineSegment(sketch, "E7.9.14.5", {"start": v(1035, 350) * mm, "end": v(1035, 405) * mm});
            skLineSegment(sketch, "E7.0.14.6", {"start": v(980, 420) * mm, "end": v(980, 475) * mm});
            skLineSegment(sketch, "E7.3.14.6", {"start": v(980, 475) * mm, "end": v(1035, 475) * mm});
            skLineSegment(sketch, "E7.6.14.6", {"start": v(980, 420) * mm, "end": v(1035, 420) * mm});
            skLineSegment(sketch, "E7.9.14.6", {"start": v(1035, 420) * mm, "end": v(1035, 475) * mm});
            skLineSegment(sketch, "E7.0.14.7", {"start": v(980, 490) * mm, "end": v(980, 545) * mm});
            skLineSegment(sketch, "E7.3.14.7", {"start": v(980, 545) * mm, "end": v(1035, 545) * mm});
            skLineSegment(sketch, "E7.6.14.7", {"start": v(980, 490) * mm, "end": v(1035, 490) * mm});
            skLineSegment(sketch, "E7.9.14.7", {"start": v(1035, 490) * mm, "end": v(1035, 545) * mm});
            skLineSegment(sketch, "E7.0.14.8", {"start": v(980, 560) * mm, "end": v(980, 615) * mm});
            skLineSegment(sketch, "E7.3.14.8", {"start": v(980, 615) * mm, "end": v(1035, 615) * mm});
            skLineSegment(sketch, "E7.6.14.8", {"start": v(980, 560) * mm, "end": v(1035, 560) * mm});
            skLineSegment(sketch, "E7.9.14.8", {"start": v(1035, 560) * mm, "end": v(1035, 615) * mm});
            skLineSegment(sketch, "E7.0.14.9", {"start": v(980, 630) * mm, "end": v(980, 685) * mm});
            skLineSegment(sketch, "E7.3.14.9", {"start": v(980, 685) * mm, "end": v(1035, 685) * mm});
            skLineSegment(sketch, "E7.6.14.9", {"start": v(980, 630) * mm, "end": v(1035, 630) * mm});
            skLineSegment(sketch, "E7.9.14.9", {"start": v(1035, 630) * mm, "end": v(1035, 685) * mm});
            skLineSegment(sketch, "E7.0.14.10", {"start": v(980, 700) * mm, "end": v(980, 755) * mm});
            skLineSegment(sketch, "E7.3.14.10", {"start": v(980, 755) * mm, "end": v(1035, 755) * mm});
            skLineSegment(sketch, "E7.6.14.10", {"start": v(980, 700) * mm, "end": v(1035, 700) * mm});
            skLineSegment(sketch, "E7.9.14.10", {"start": v(1035, 700) * mm, "end": v(1035, 755) * mm});
            skLineSegment(sketch, "E7.0.14.11", {"start": v(980, 770) * mm, "end": v(980, 825) * mm});
            skLineSegment(sketch, "E7.3.14.11", {"start": v(980, 825) * mm, "end": v(1035, 825) * mm});
            skLineSegment(sketch, "E7.6.14.11", {"start": v(980, 770) * mm, "end": v(1035, 770) * mm});
            skLineSegment(sketch, "E7.9.14.11", {"start": v(1035, 770) * mm, "end": v(1035, 825) * mm});
            skLineSegment(sketch, "E8.0.0.12", {"start": v(0, 840) * mm, "end": v(0, 895) * mm});
            skLineSegment(sketch, "E8.3.0.12", {"start": v(0, 895) * mm, "end": v(55, 895) * mm});
            skLineSegment(sketch, "E8.6.0.12", {"start": v(0, 840) * mm, "end": v(55, 840) * mm});
            skLineSegment(sketch, "E8.9.0.12", {"start": v(55, 840) * mm, "end": v(55, 895) * mm});
            skLineSegment(sketch, "E8.0.0.13", {"start": v(0, 910) * mm, "end": v(0, 965) * mm});
            skLineSegment(sketch, "E8.3.0.13", {"start": v(0, 965) * mm, "end": v(55, 965) * mm});
            skLineSegment(sketch, "E8.6.0.13", {"start": v(0, 910) * mm, "end": v(55, 910) * mm});
            skLineSegment(sketch, "E8.9.0.13", {"start": v(55, 910) * mm, "end": v(55, 965) * mm});
            skLineSegment(sketch, "E8.0.0.14", {"start": v(0, 980) * mm, "end": v(0, 1035) * mm});
            skLineSegment(sketch, "E8.3.0.14", {"start": v(0, 1035) * mm, "end": v(55, 1035) * mm});
            skLineSegment(sketch, "E8.6.0.14", {"start": v(0, 980) * mm, "end": v(55, 980) * mm});
            skLineSegment(sketch, "E8.9.0.14", {"start": v(55, 980) * mm, "end": v(55, 1035) * mm});
            skLineSegment(sketch, "E8.0.1.12", {"start": v(70, 840) * mm, "end": v(70, 895) * mm});
            skLineSegment(sketch, "E8.3.1.12", {"start": v(70, 895) * mm, "end": v(125, 895) * mm});
            skLineSegment(sketch, "E8.6.1.12", {"start": v(70, 840) * mm, "end": v(125, 840) * mm});
            skLineSegment(sketch, "E8.9.1.12", {"start": v(125, 840) * mm, "end": v(125, 895) * mm});
            skLineSegment(sketch, "E8.0.1.13", {"start": v(70, 910) * mm, "end": v(70, 965) * mm});
            skLineSegment(sketch, "E8.3.1.13", {"start": v(70, 965) * mm, "end": v(125, 965) * mm});
            skLineSegment(sketch, "E8.6.1.13", {"start": v(70, 910) * mm, "end": v(125, 910) * mm});
            skLineSegment(sketch, "E8.9.1.13", {"start": v(125, 910) * mm, "end": v(125, 965) * mm});
            skLineSegment(sketch, "E8.0.1.14", {"start": v(70, 980) * mm, "end": v(70, 1035) * mm});
            skLineSegment(sketch, "E8.3.1.14", {"start": v(70, 1035) * mm, "end": v(125, 1035) * mm});
            skLineSegment(sketch, "E8.6.1.14", {"start": v(70, 980) * mm, "end": v(125, 980) * mm});
            skLineSegment(sketch, "E8.9.1.14", {"start": v(125, 980) * mm, "end": v(125, 1035) * mm});
            skLineSegment(sketch, "E8.0.2.12", {"start": v(140, 840) * mm, "end": v(140, 895) * mm});
            skLineSegment(sketch, "E8.3.2.12", {"start": v(140, 895) * mm, "end": v(195, 895) * mm});
            skLineSegment(sketch, "E8.6.2.12", {"start": v(140, 840) * mm, "end": v(195, 840) * mm});
            skLineSegment(sketch, "E8.9.2.12", {"start": v(195, 840) * mm, "end": v(195, 895) * mm});
            skLineSegment(sketch, "E8.0.2.13", {"start": v(140, 910) * mm, "end": v(140, 965) * mm});
            skLineSegment(sketch, "E8.3.2.13", {"start": v(140, 965) * mm, "end": v(195, 965) * mm});
            skLineSegment(sketch, "E8.6.2.13", {"start": v(140, 910) * mm, "end": v(195, 910) * mm});
            skLineSegment(sketch, "E8.9.2.13", {"start": v(195, 910) * mm, "end": v(195, 965) * mm});
            skLineSegment(sketch, "E8.0.2.14", {"start": v(140, 980) * mm, "end": v(140, 1035) * mm});
            skLineSegment(sketch, "E8.3.2.14", {"start": v(140, 1035) * mm, "end": v(195, 1035) * mm});
            skLineSegment(sketch, "E8.6.2.14", {"start": v(140, 980) * mm, "end": v(195, 980) * mm});
            skLineSegment(sketch, "E8.9.2.14", {"start": v(195, 980) * mm, "end": v(195, 1035) * mm});
            skLineSegment(sketch, "E8.0.3.12", {"start": v(210, 840) * mm, "end": v(210, 895) * mm});
            skLineSegment(sketch, "E8.3.3.12", {"start": v(210, 895) * mm, "end": v(265, 895) * mm});
            skLineSegment(sketch, "E8.6.3.12", {"start": v(210, 840) * mm, "end": v(265, 840) * mm});
            skLineSegment(sketch, "E8.9.3.12", {"start": v(265, 840) * mm, "end": v(265, 895) * mm});
            skLineSegment(sketch, "E8.0.3.13", {"start": v(210, 910) * mm, "end": v(210, 965) * mm});
            skLineSegment(sketch, "E8.3.3.13", {"start": v(210, 965) * mm, "end": v(265, 965) * mm});
            skLineSegment(sketch, "E8.6.3.13", {"start": v(210, 910) * mm, "end": v(265, 910) * mm});
            skLineSegment(sketch, "E8.9.3.13", {"start": v(265, 910) * mm, "end": v(265, 965) * mm});
            skLineSegment(sketch, "E8.0.3.14", {"start": v(210, 980) * mm, "end": v(210, 1035) * mm});
            skLineSegment(sketch, "E8.3.3.14", {"start": v(210, 1035) * mm, "end": v(265, 1035) * mm});
            skLineSegment(sketch, "E8.6.3.14", {"start": v(210, 980) * mm, "end": v(265, 980) * mm});
            skLineSegment(sketch, "E8.9.3.14", {"start": v(265, 980) * mm, "end": v(265, 1035) * mm});
            skLineSegment(sketch, "E8.0.4.12", {"start": v(280, 840) * mm, "end": v(280, 895) * mm});
            skLineSegment(sketch, "E8.3.4.12", {"start": v(280, 895) * mm, "end": v(335, 895) * mm});
            skLineSegment(sketch, "E8.6.4.12", {"start": v(280, 840) * mm, "end": v(335, 840) * mm});
            skLineSegment(sketch, "E8.9.4.12", {"start": v(335, 840) * mm, "end": v(335, 895) * mm});
            skLineSegment(sketch, "E8.0.4.13", {"start": v(280, 910) * mm, "end": v(280, 965) * mm});
            skLineSegment(sketch, "E8.3.4.13", {"start": v(280, 965) * mm, "end": v(335, 965) * mm});
            skLineSegment(sketch, "E8.6.4.13", {"start": v(280, 910) * mm, "end": v(335, 910) * mm});
            skLineSegment(sketch, "E8.9.4.13", {"start": v(335, 910) * mm, "end": v(335, 965) * mm});
            skLineSegment(sketch, "E8.0.4.14", {"start": v(280, 980) * mm, "end": v(280, 1035) * mm});
            skLineSegment(sketch, "E8.3.4.14", {"start": v(280, 1035) * mm, "end": v(335, 1035) * mm});
            skLineSegment(sketch, "E8.6.4.14", {"start": v(280, 980) * mm, "end": v(335, 980) * mm});
            skLineSegment(sketch, "E8.9.4.14", {"start": v(335, 980) * mm, "end": v(335, 1035) * mm});
            skLineSegment(sketch, "E8.0.5.12", {"start": v(350, 840) * mm, "end": v(350, 895) * mm});
            skLineSegment(sketch, "E8.3.5.12", {"start": v(350, 895) * mm, "end": v(405, 895) * mm});
            skLineSegment(sketch, "E8.6.5.12", {"start": v(350, 840) * mm, "end": v(405, 840) * mm});
            skLineSegment(sketch, "E8.9.5.12", {"start": v(405, 840) * mm, "end": v(405, 895) * mm});
            skLineSegment(sketch, "E8.0.5.13", {"start": v(350, 910) * mm, "end": v(350, 965) * mm});
            skLineSegment(sketch, "E8.3.5.13", {"start": v(350, 965) * mm, "end": v(405, 965) * mm});
            skLineSegment(sketch, "E8.6.5.13", {"start": v(350, 910) * mm, "end": v(405, 910) * mm});
            skLineSegment(sketch, "E8.9.5.13", {"start": v(405, 910) * mm, "end": v(405, 965) * mm});
            skLineSegment(sketch, "E8.0.5.14", {"start": v(350, 980) * mm, "end": v(350, 1035) * mm});
            skLineSegment(sketch, "E8.3.5.14", {"start": v(350, 1035) * mm, "end": v(405, 1035) * mm});
            skLineSegment(sketch, "E8.6.5.14", {"start": v(350, 980) * mm, "end": v(405, 980) * mm});
            skLineSegment(sketch, "E8.9.5.14", {"start": v(405, 980) * mm, "end": v(405, 1035) * mm});
            skLineSegment(sketch, "E8.0.6.12", {"start": v(420, 840) * mm, "end": v(420, 895) * mm});
            skLineSegment(sketch, "E8.3.6.12", {"start": v(420, 895) * mm, "end": v(475, 895) * mm});
            skLineSegment(sketch, "E8.6.6.12", {"start": v(420, 840) * mm, "end": v(475, 840) * mm});
            skLineSegment(sketch, "E8.9.6.12", {"start": v(475, 840) * mm, "end": v(475, 895) * mm});
            skLineSegment(sketch, "E8.0.6.13", {"start": v(420, 910) * mm, "end": v(420, 965) * mm});
            skLineSegment(sketch, "E8.3.6.13", {"start": v(420, 965) * mm, "end": v(475, 965) * mm});
            skLineSegment(sketch, "E8.6.6.13", {"start": v(420, 910) * mm, "end": v(475, 910) * mm});
            skLineSegment(sketch, "E8.9.6.13", {"start": v(475, 910) * mm, "end": v(475, 965) * mm});
            skLineSegment(sketch, "E8.0.6.14", {"start": v(420, 980) * mm, "end": v(420, 1035) * mm});
            skLineSegment(sketch, "E8.3.6.14", {"start": v(420, 1035) * mm, "end": v(475, 1035) * mm});
            skLineSegment(sketch, "E8.6.6.14", {"start": v(420, 980) * mm, "end": v(475, 980) * mm});
            skLineSegment(sketch, "E8.9.6.14", {"start": v(475, 980) * mm, "end": v(475, 1035) * mm});
            skLineSegment(sketch, "E8.0.7.12", {"start": v(490, 840) * mm, "end": v(490, 895) * mm});
            skLineSegment(sketch, "E8.3.7.12", {"start": v(490, 895) * mm, "end": v(545, 895) * mm});
            skLineSegment(sketch, "E8.6.7.12", {"start": v(490, 840) * mm, "end": v(545, 840) * mm});
            skLineSegment(sketch, "E8.9.7.12", {"start": v(545, 840) * mm, "end": v(545, 895) * mm});
            skLineSegment(sketch, "E8.0.7.13", {"start": v(490, 910) * mm, "end": v(490, 965) * mm});
            skLineSegment(sketch, "E8.3.7.13", {"start": v(490, 965) * mm, "end": v(545, 965) * mm});
            skLineSegment(sketch, "E8.6.7.13", {"start": v(490, 910) * mm, "end": v(545, 910) * mm});
            skLineSegment(sketch, "E8.9.7.13", {"start": v(545, 910) * mm, "end": v(545, 965) * mm});
            skLineSegment(sketch, "E8.0.7.14", {"start": v(490, 980) * mm, "end": v(490, 1035) * mm});
            skLineSegment(sketch, "E8.3.7.14", {"start": v(490, 1035) * mm, "end": v(545, 1035) * mm});
            skLineSegment(sketch, "E8.6.7.14", {"start": v(490, 980) * mm, "end": v(545, 980) * mm});
            skLineSegment(sketch, "E8.9.7.14", {"start": v(545, 980) * mm, "end": v(545, 1035) * mm});
            skLineSegment(sketch, "E8.0.8.12", {"start": v(560, 840) * mm, "end": v(560, 895) * mm});
            skLineSegment(sketch, "E8.3.8.12", {"start": v(560, 895) * mm, "end": v(615, 895) * mm});
            skLineSegment(sketch, "E8.6.8.12", {"start": v(560, 840) * mm, "end": v(615, 840) * mm});
            skLineSegment(sketch, "E8.9.8.12", {"start": v(615, 840) * mm, "end": v(615, 895) * mm});
            skLineSegment(sketch, "E8.0.8.13", {"start": v(560, 910) * mm, "end": v(560, 965) * mm});
            skLineSegment(sketch, "E8.3.8.13", {"start": v(560, 965) * mm, "end": v(615, 965) * mm});
            skLineSegment(sketch, "E8.6.8.13", {"start": v(560, 910) * mm, "end": v(615, 910) * mm});
            skLineSegment(sketch, "E8.9.8.13", {"start": v(615, 910) * mm, "end": v(615, 965) * mm});
            skLineSegment(sketch, "E8.0.8.14", {"start": v(560, 980) * mm, "end": v(560, 1035) * mm});
            skLineSegment(sketch, "E8.3.8.14", {"start": v(560, 1035) * mm, "end": v(615, 1035) * mm});
            skLineSegment(sketch, "E8.6.8.14", {"start": v(560, 980) * mm, "end": v(615, 980) * mm});
            skLineSegment(sketch, "E8.9.8.14", {"start": v(615, 980) * mm, "end": v(615, 1035) * mm});
            skLineSegment(sketch, "E8.0.9.12", {"start": v(630, 840) * mm, "end": v(630, 895) * mm});
            skLineSegment(sketch, "E8.3.9.12", {"start": v(630, 895) * mm, "end": v(685, 895) * mm});
            skLineSegment(sketch, "E8.6.9.12", {"start": v(630, 840) * mm, "end": v(685, 840) * mm});
            skLineSegment(sketch, "E8.9.9.12", {"start": v(685, 840) * mm, "end": v(685, 895) * mm});
            skLineSegment(sketch, "E8.0.9.13", {"start": v(630, 910) * mm, "end": v(630, 965) * mm});
            skLineSegment(sketch, "E8.3.9.13", {"start": v(630, 965) * mm, "end": v(685, 965) * mm});
            skLineSegment(sketch, "E8.6.9.13", {"start": v(630, 910) * mm, "end": v(685, 910) * mm});
            skLineSegment(sketch, "E8.9.9.13", {"start": v(685, 910) * mm, "end": v(685, 965) * mm});
            skLineSegment(sketch, "E8.0.9.14", {"start": v(630, 980) * mm, "end": v(630, 1035) * mm});
            skLineSegment(sketch, "E8.3.9.14", {"start": v(630, 1035) * mm, "end": v(685, 1035) * mm});
            skLineSegment(sketch, "E8.6.9.14", {"start": v(630, 980) * mm, "end": v(685, 980) * mm});
            skLineSegment(sketch, "E8.9.9.14", {"start": v(685, 980) * mm, "end": v(685, 1035) * mm});
            skLineSegment(sketch, "E8.0.10.12", {"start": v(700, 840) * mm, "end": v(700, 895) * mm});
            skLineSegment(sketch, "E8.3.10.12", {"start": v(700, 895) * mm, "end": v(755, 895) * mm});
            skLineSegment(sketch, "E8.6.10.12", {"start": v(700, 840) * mm, "end": v(755, 840) * mm});
            skLineSegment(sketch, "E8.9.10.12", {"start": v(755, 840) * mm, "end": v(755, 895) * mm});
            skLineSegment(sketch, "E8.0.10.13", {"start": v(700, 910) * mm, "end": v(700, 965) * mm});
            skLineSegment(sketch, "E8.3.10.13", {"start": v(700, 965) * mm, "end": v(755, 965) * mm});
            skLineSegment(sketch, "E8.6.10.13", {"start": v(700, 910) * mm, "end": v(755, 910) * mm});
            skLineSegment(sketch, "E8.9.10.13", {"start": v(755, 910) * mm, "end": v(755, 965) * mm});
            skLineSegment(sketch, "E8.0.10.14", {"start": v(700, 980) * mm, "end": v(700, 1035) * mm});
            skLineSegment(sketch, "E8.3.10.14", {"start": v(700, 1035) * mm, "end": v(755, 1035) * mm});
            skLineSegment(sketch, "E8.6.10.14", {"start": v(700, 980) * mm, "end": v(755, 980) * mm});
            skLineSegment(sketch, "E8.9.10.14", {"start": v(755, 980) * mm, "end": v(755, 1035) * mm});
            skLineSegment(sketch, "E8.0.11.12", {"start": v(770, 840) * mm, "end": v(770, 895) * mm});
            skLineSegment(sketch, "E8.3.11.12", {"start": v(770, 895) * mm, "end": v(825, 895) * mm});
            skLineSegment(sketch, "E8.6.11.12", {"start": v(770, 840) * mm, "end": v(825, 840) * mm});
            skLineSegment(sketch, "E8.9.11.12", {"start": v(825, 840) * mm, "end": v(825, 895) * mm});
            skLineSegment(sketch, "E8.0.11.13", {"start": v(770, 910) * mm, "end": v(770, 965) * mm});
            skLineSegment(sketch, "E8.3.11.13", {"start": v(770, 965) * mm, "end": v(825, 965) * mm});
            skLineSegment(sketch, "E8.6.11.13", {"start": v(770, 910) * mm, "end": v(825, 910) * mm});
            skLineSegment(sketch, "E8.9.11.13", {"start": v(825, 910) * mm, "end": v(825, 965) * mm});
            skLineSegment(sketch, "E8.0.11.14", {"start": v(770, 980) * mm, "end": v(770, 1035) * mm});
            skLineSegment(sketch, "E8.3.11.14", {"start": v(770, 1035) * mm, "end": v(825, 1035) * mm});
            skLineSegment(sketch, "E8.6.11.14", {"start": v(770, 980) * mm, "end": v(825, 980) * mm});
            skLineSegment(sketch, "E8.9.11.14", {"start": v(825, 980) * mm, "end": v(825, 1035) * mm});
            skLineSegment(sketch, "E8.0.12.12", {"start": v(840, 840) * mm, "end": v(840, 895) * mm});
            skLineSegment(sketch, "E8.3.12.12", {"start": v(840, 895) * mm, "end": v(895, 895) * mm});
            skLineSegment(sketch, "E8.6.12.12", {"start": v(840, 840) * mm, "end": v(895, 840) * mm});
            skLineSegment(sketch, "E8.9.12.12", {"start": v(895, 840) * mm, "end": v(895, 895) * mm});
            skLineSegment(sketch, "E8.0.12.13", {"start": v(840, 910) * mm, "end": v(840, 965) * mm});
            skLineSegment(sketch, "E8.3.12.13", {"start": v(840, 965) * mm, "end": v(895, 965) * mm});
            skLineSegment(sketch, "E8.6.12.13", {"start": v(840, 910) * mm, "end": v(895, 910) * mm});
            skLineSegment(sketch, "E8.9.12.13", {"start": v(895, 910) * mm, "end": v(895, 965) * mm});
            skLineSegment(sketch, "E8.0.12.14", {"start": v(840, 980) * mm, "end": v(840, 1035) * mm});
            skLineSegment(sketch, "E8.3.12.14", {"start": v(840, 1035) * mm, "end": v(895, 1035) * mm});
            skLineSegment(sketch, "E8.6.12.14", {"start": v(840, 980) * mm, "end": v(895, 980) * mm});
            skLineSegment(sketch, "E8.9.12.14", {"start": v(895, 980) * mm, "end": v(895, 1035) * mm});
            skLineSegment(sketch, "E8.0.13.12", {"start": v(910, 840) * mm, "end": v(910, 895) * mm});
            skLineSegment(sketch, "E8.3.13.12", {"start": v(910, 895) * mm, "end": v(965, 895) * mm});
            skLineSegment(sketch, "E8.6.13.12", {"start": v(910, 840) * mm, "end": v(965, 840) * mm});
            skLineSegment(sketch, "E8.9.13.12", {"start": v(965, 840) * mm, "end": v(965, 895) * mm});
            skLineSegment(sketch, "E8.0.13.13", {"start": v(910, 910) * mm, "end": v(910, 965) * mm});
            skLineSegment(sketch, "E8.3.13.13", {"start": v(910, 965) * mm, "end": v(965, 965) * mm});
            skLineSegment(sketch, "E8.6.13.13", {"start": v(910, 910) * mm, "end": v(965, 910) * mm});
            skLineSegment(sketch, "E8.9.13.13", {"start": v(965, 910) * mm, "end": v(965, 965) * mm});
            skLineSegment(sketch, "E8.0.13.14", {"start": v(910, 980) * mm, "end": v(910, 1035) * mm});
            skLineSegment(sketch, "E8.3.13.14", {"start": v(910, 1035) * mm, "end": v(965, 1035) * mm});
            skLineSegment(sketch, "E8.6.13.14", {"start": v(910, 980) * mm, "end": v(965, 980) * mm});
            skLineSegment(sketch, "E8.9.13.14", {"start": v(965, 980) * mm, "end": v(965, 1035) * mm});
            skLineSegment(sketch, "E8.0.14.12", {"start": v(980, 840) * mm, "end": v(980, 895) * mm});
            skLineSegment(sketch, "E8.3.14.12", {"start": v(980, 895) * mm, "end": v(1035, 895) * mm});
            skLineSegment(sketch, "E8.6.14.12", {"start": v(980, 840) * mm, "end": v(1035, 840) * mm});
            skLineSegment(sketch, "E8.9.14.12", {"start": v(1035, 840) * mm, "end": v(1035, 895) * mm});
            skLineSegment(sketch, "E8.0.14.13", {"start": v(980, 910) * mm, "end": v(980, 965) * mm});
            skLineSegment(sketch, "E8.3.14.13", {"start": v(980, 965) * mm, "end": v(1035, 965) * mm});
            skLineSegment(sketch, "E8.6.14.13", {"start": v(980, 910) * mm, "end": v(1035, 910) * mm});
            skLineSegment(sketch, "E8.9.14.13", {"start": v(1035, 910) * mm, "end": v(1035, 965) * mm});
            skLineSegment(sketch, "E8.0.14.14", {"start": v(980, 980) * mm, "end": v(980, 1035) * mm});
            skLineSegment(sketch, "E8.3.14.14", {"start": v(980, 1035) * mm, "end": v(1035, 1035) * mm});
            skLineSegment(sketch, "E8.6.14.14", {"start": v(980, 980) * mm, "end": v(1035, 980) * mm});
            skLineSegment(sketch, "E8.9.14.14", {"start": v(1035, 980) * mm, "end": v(1035, 1035) * mm});
            skSolve(sketch);
        }
        {
            var Q0;
            Q0=makeQuery(id+"F0.imprint","IMPRINT",FACE,{"disambiguationData":[TD([[makeQuery(id+"F0.imprint","IMPRINT",EDGE,{"derivedFrom":sQuery(id+"F0.wireOp",EDGE,"E0.bottom")}),-1.0]])]});
            extrude(context, id + "F1", {"entities" : qUnion([Q0]), "depth" : 1 * mm, "offsetDistance" : 25 * mm});
        }
    });
